FCSTD DOCUMENT  (FreeCAD 1.0R39109 (Git))
Label: tip-etcher_v2]
License: All rights reserved
objects: App::Link×91, App::FeaturePython×20, Assembly::AssemblyLink×10, Assembly::JointGroup×1, Assembly::AssemblyObject×1
EXTERNAL_REF file=power-supply/psu-mount.FCStd obj=Assembly
EXTERNAL_REF file=power-supply/psu-mount.FCStd obj=mount
EXTERNAL_REF file=power-supply/psu-mount.FCStd obj=M3x5_74_Insert
EXTERNAL_REF file=power-supply/psu-mount.FCStd obj=M3x5_74_Insert001
EXTERNAL_REF file=power-supply/psu-mount.FCStd obj=M5x10_Screw
EXTERNAL_REF file=power-supply/psu-mount.FCStd obj=M5x10_Screw002
EXTERNAL_REF file=power-supply/psu-mount.FCStd obj=M5x10_Screw003
EXTERNAL_REF file=power-supply/psu-mount.FCStd obj=M5x10_Screw004
EXTERNAL_REF file=power-supply/psu-mount.FCStd obj=M5x10_Screw005
EXTERNAL_REF file=power-supply/psu-mount.FCStd obj=M5x10_Screw006
EXTERNAL_REF file=power-supply/psu-mount.FCStd obj=M5x10_Screw007
EXTERNAL_REF file=power-supply/psu-mount.FCStd obj=M5x10_Screw008
EXTERNAL_REF file=power-supply/psu-mount.FCStd obj=MW_LRS_50_24
EXTERNAL_REF file=power-supply/psu-mount.FCStd obj=M3x6_Screw
EXTERNAL_REF file=power-supply/psu-mount.FCStd obj=M3x6_Screw001
EXTERNAL_REF file=frame/assembly-frame.FCStd obj=Assembly
EXTERNAL_REF file=frame/assembly-frame.FCStd obj=_020_150mm_v2
EXTERNAL_REF file=frame/assembly-frame.FCStd obj=_020_150mm_v003
EXTERNAL_REF file=frame/assembly-frame.FCStd obj=_020_150mm_v004
EXTERNAL_REF file=frame/assembly-frame.FCStd obj=_020_150mm_v005
EXTERNAL_REF file=frame/assembly-frame.FCStd obj=_020_250mm_v2
EXTERNAL_REF file=frame/assembly-frame.FCStd obj=_020_250mm_v003
EXTERNAL_REF file=frame/assembly-frame.FCStd obj=_020_250mm_v004
EXTERNAL_REF file=frame/assembly-frame.FCStd obj=_020_150mm_v006
EXTERNAL_REF file=frame/assembly-frame.FCStd obj=_020_150mm_v007
EXTERNAL_REF file=frame/assembly-frame.FCStd obj=_020_150mm_v008
EXTERNAL_REF file=frame/assembly-frame.FCStd obj=_020_150mm_v009
EXTERNAL_REF file=frame/L-mount.FCStd obj=Assembly
EXTERNAL_REF file=frame/L-mount.FCStd obj=Body001
EXTERNAL_REF file=frame/L-mount.FCStd obj=M5x10_Screw
EXTERNAL_REF file=frame/L-mount.FCStd obj=M5x10_Screw001
EXTERNAL_REF file=frame/L-mount.FCStd obj=M5x10_Screw002
EXTERNAL_REF file=frame/L-mount.FCStd obj=M5x10_Screw003
EXTERNAL_REF file=frame/L-mount.FCStd obj=M5x10_Screw004
EXTERNAL_REF file=frame/L-mount.FCStd obj=M5x10_Screw005
EXTERNAL_REF file=frame/corner-mount.FCStd obj=Assembly
EXTERNAL_REF file=frame/corner-mount.FCStd obj=M5x10_Screw
EXTERNAL_REF file=frame/corner-mount.FCStd obj=Body001
EXTERNAL_REF file=frame/corner-mount.FCStd obj=M5x10_Screw001
EXTERNAL_REF file=frame/corner-mount.FCStd obj=M5x10_Screw002
EXTERNAL_REF file=frame/corner-mount.FCStd obj=M5x10_Screw003
EXTERNAL_REF file=frame/corner-mount.FCStd obj=M5x10_Screw004
EXTERNAL_REF file=frame/corner-mount.FCStd obj=M5x10_Screw005
EXTERNAL_REF file=mechanism/base.FCStd obj=Body
EXTERNAL_REF file=mechanism/rod.FCStd obj=Body
EXTERNAL_REF file=mechanism/head.FCStd obj=Body
EXTERNAL_REF file=mechanism/top.FCStd obj=Body
EXTERNAL_REF file=mechanism/stm_mount.FCStd obj=Body
EXTERNAL_REF file=mechanism/profile_cover.FCStd obj=Body
EXTERNAL_REF file=mechanism/funnel.FCStd obj=Body
EXTERNAL_REF file=mechanism/bearing_holder.FCStd obj=Body
EXTERNAL_REF file=Screen/Screen_v3.FCStd obj=Body

FEATURE [App::Link] mount  label="mount001"
  LinkedObject = -> <external power-supply/psu-mount.FCStd>#mount
FEATURE [App::Link] M3x5_74_Insert  label="M3x5.74-Insert001"
  LinkPlacement = pos=(48,110,10.0967) rot=(0,0,1;0rad)
  LinkedObject = -> <external power-supply/psu-mount.FCStd>#M3x5_74_Insert
  Placement = pos=(48,110,10.0967) rot=(0,0,1;0rad)
FEATURE [App::Link] M3x5_74_Insert001  label="M3x5.74-Insert002"
  LinkPlacement = pos=(140.5,40,10.0967) rot=(0,0,1;0rad)
  LinkedObject = -> <external power-supply/psu-mount.FCStd>#M3x5_74_Insert001
  Placement = pos=(140.5,40,10.0967) rot=(0,0,1;0rad)
FEATURE [App::Link] M5x10_Screw  label="M5x10-Screw001"
  LinkPlacement = pos=(68.5,10.5,0) rot=(1,0,0;3.14159rad)
  LinkedObject = -> <external power-supply/psu-mount.FCStd>#M5x10_Screw
  Placement = pos=(68.5,10.5,0) rot=(1,0,0;3.14159rad)
FEATURE [App::Link] M5x10_Screw002  label="M5x10-Screw003"
  LinkPlacement = pos=(179.5,58.5,0) rot=(1,0,0;3.14159rad)
  LinkedObject = -> <external power-supply/psu-mount.FCStd>#M5x10_Screw002
  Placement = pos=(179.5,58.5,0) rot=(1,0,0;3.14159rad)
FEATURE [App::Link] M5x10_Screw003  label="M5x10-Screw004"
  LinkPlacement = pos=(179.5,91.5,0) rot=(1,0,0;3.14159rad)
  LinkedObject = -> <external power-supply/psu-mount.FCStd>#M5x10_Screw003
  Placement = pos=(179.5,91.5,0) rot=(1,0,0;3.14159rad)
FEATURE [App::Link] M5x10_Screw004  label="M5x10-Screw005"
  LinkPlacement = pos=(121.5,139.5,0) rot=(1,0,0;3.14159rad)
  LinkedObject = -> <external power-supply/psu-mount.FCStd>#M5x10_Screw004
  Placement = pos=(121.5,139.5,0) rot=(1,0,0;3.14159rad)
FEATURE [App::Link] M5x10_Screw005  label="M5x10-Screw006"
  LinkPlacement = pos=(68.5,139.5,0) rot=(1,0,0;3.14159rad)
  LinkedObject = -> <external power-supply/psu-mount.FCStd>#M5x10_Screw005
  Placement = pos=(68.5,139.5,0) rot=(1,0,0;3.14159rad)
FEATURE [App::Link] M5x10_Screw006  label="M5x10-Screw007"
  LinkPlacement = pos=(10.5,58.5,0) rot=(1,0,0;3.14159rad)
  LinkedObject = -> <external power-supply/psu-mount.FCStd>#M5x10_Screw006
  Placement = pos=(10.5,58.5,0) rot=(1,0,0;3.14159rad)
FEATURE [App::Link] M5x10_Screw007  label="M5x10-Screw008"
  LinkPlacement = pos=(10.5,91.5,0) rot=(1,0,0;3.14159rad)
  LinkedObject = -> <external power-supply/psu-mount.FCStd>#M5x10_Screw007
  Placement = pos=(10.5,91.5,0) rot=(1,0,0;3.14159rad)
FEATURE [App::Link] M5x10_Screw008  label="M5x10-Screw009"
  LinkPlacement = pos=(121.5,10.5,0) rot=(1,0,0;3.14159rad)
  LinkedObject = -> <external power-supply/psu-mount.FCStd>#M5x10_Screw008
  Placement = pos=(121.5,10.5,0) rot=(1,0,0;3.14159rad)
FEATURE [App::Link] MW_LRS_50_24  label="MW LRS-50-025"
  LinkPlacement = pos=(43.5,33.5,10) rot=(1,0,0;1.5708rad)
  LinkedObject = -> <external power-supply/psu-mount.FCStd>#MW_LRS_50_24
  Placement = pos=(43.5,33.5,10) rot=(1,0,0;1.5708rad)
FEATURE [App::Link] M3x6_Screw  label="M3x6-Screw001"
  LinkPlacement = pos=(48,110,11) rot=(0,0,1;4.71239rad)
  LinkedObject = -> <external power-supply/psu-mount.FCStd>#M3x6_Screw
  Placement = pos=(48,110,11) rot=(0,0,1;4.71239rad)
FEATURE [App::Link] M3x6_Screw001  label="M3x6-Screw002"
  LinkPlacement = pos=(140.5,40,11) rot=(0,0,-1;1.5708rad)
  LinkedObject = -> <external power-supply/psu-mount.FCStd>#M3x6_Screw001
  Placement = pos=(140.5,40,11) rot=(0,0,-1;1.5708rad)
FEATURE [Assembly::AssemblyLink] psu_mount  label="psu-mount"
  Group = -> [mount,M3x5_74_Insert,M3x5_74_Insert001,M5x10_Screw,M5x10_Screw002,M5x10_Screw003,M5x10_Screw004,M5x10_Screw005,M5x10_Screw006,M5x10_Screw007,M5x10_Screw008,MW_LRS_50_24,M3x6_Screw,M3x6_Screw001]
  LinkedObject = -> <external power-supply/psu-mount.FCStd>#Assembly
  Origin = -> Origin001
  Placement = pos=(-9.50002,14,-3.8147e-06) rot=(1,0,0;1.5708rad)
  Rigid = true
FEATURE [App::Link] _020_150mm_v2  label="2020_150mm_001"
  LinkedObject = -> <external frame/assembly-frame.FCStd>#_020_150mm_v2
FEATURE [App::Link] _020_150mm_v003  label="2020_150mm_002"
  LinkPlacement = pos=(160,1.8e-15,140) rot=(0,-1,0;1.5708rad)
  LinkedObject = -> <external frame/assembly-frame.FCStd>#_020_150mm_v003
  Placement = pos=(160,1.8e-15,140) rot=(0,-1,0;1.5708rad)
FEATURE [App::Link] _020_150mm_v004  label="2020_150mm_003"
  LinkPlacement = pos=(170,3.64e-14,-2.49e-14) rot=(0,0,1;0rad)
  LinkedObject = -> <external frame/assembly-frame.FCStd>#_020_150mm_v004
  Placement = pos=(170,3.64e-14,-2.49e-14) rot=(0,0,1;0rad)
FEATURE [App::Link] _020_150mm_v005  label="2020_150mm_004"
  LinkPlacement = pos=(160,2.7e-15,10) rot=(0,1,0;4.71239rad)
  LinkedObject = -> <external frame/assembly-frame.FCStd>#_020_150mm_v005
  Placement = pos=(160,2.7e-15,10) rot=(0,1,0;4.71239rad)
FEATURE [App::Link] _020_250mm_v2  label="2020_250mm_001"
  LinkPlacement = pos=(-1.101e-13,-260,10) rot=(-1,0,0;1.5708rad)
  LinkedObject = -> <external frame/assembly-frame.FCStd>#_020_250mm_v2
  Placement = pos=(-1.101e-13,-260,10) rot=(-1,0,0;1.5708rad)
FEATURE [App::Link] _020_250mm_v003  label="2020_250mm_002"
  LinkPlacement = pos=(1.11e-13,-260,140) rot=(1,0,0;4.71239rad)
  LinkedObject = -> <external frame/assembly-frame.FCStd>#_020_250mm_v003
  Placement = pos=(1.11e-13,-260,140) rot=(1,0,0;4.71239rad)
FEATURE [App::Link] _020_250mm_v004  label="2020_250mm_003"
  LinkPlacement = pos=(170,-260,10) rot=(-1,0,0;1.5708rad)
  LinkedObject = -> <external frame/assembly-frame.FCStd>#_020_250mm_v004
  Placement = pos=(170,-260,10) rot=(-1,0,0;1.5708rad)
FEATURE [App::Link] _020_150mm_v006  label="2020_150mm_005"
  LinkPlacement = pos=(1.814e-13,-270,7.13e-14) rot=(0,0,1;0rad)
  LinkedObject = -> <external frame/assembly-frame.FCStd>#_020_150mm_v006
  Placement = pos=(1.814e-13,-270,7.13e-14) rot=(0,0,1;0rad)
FEATURE [App::Link] _020_150mm_v007  label="2020_150mm_006"
  LinkPlacement = pos=(10,-270,140) rot=(0,1,0;1.5708rad)
  LinkedObject = -> <external frame/assembly-frame.FCStd>#_020_150mm_v007
  Placement = pos=(10,-270,140) rot=(0,1,0;1.5708rad)
FEATURE [App::Link] _020_150mm_v008  label="2020_150mm_007"
  LinkPlacement = pos=(170,-270,150) rot=(1,0,0;3.14159rad)
  LinkedObject = -> <external frame/assembly-frame.FCStd>#_020_150mm_v008
  Placement = pos=(170,-270,150) rot=(1,0,0;3.14159rad)
FEATURE [App::Link] _020_150mm_v009  label="2020_150mm_008"
  LinkPlacement = pos=(10,-270,10) rot=(0,1,0;1.5708rad)
  LinkedObject = -> <external frame/assembly-frame.FCStd>#_020_150mm_v009
  Placement = pos=(10,-270,10) rot=(0,1,0;1.5708rad)
FEATURE [Assembly::AssemblyLink] frame
  Group = -> [_020_150mm_v2,_020_150mm_v003,_020_150mm_v004,_020_150mm_v005,_020_250mm_v2,_020_250mm_v003,_020_250mm_v004,_020_150mm_v006,_020_150mm_v007,_020_150mm_v008,_020_150mm_v009]
  LinkedObject = -> <external frame/assembly-frame.FCStd>#Assembly
  Origin = -> Origin002
  Placement = pos=(-1.52588e-05,1.52588e-05,-3.8147e-06) rot=(0,0,1;0rad)
  Rigid = true
FEATURE [App::Link] Body001
  LinkedObject = -> <external frame/L-mount.FCStd>#Body001
FEATURE [App::Link] M5x10_Screw009  label="M5x10-Screw010"
  LinkPlacement = pos=(14,34,0) rot=(1,0,0;3.14159rad)
  LinkedObject = -> <external frame/L-mount.FCStd>#M5x10_Screw
  Placement = pos=(14,34,0) rot=(1,0,0;3.14159rad)
FEATURE [App::Link] M5x10_Screw001  label="M5x10-Screw002"
  LinkPlacement = pos=(28.2,34,14) rot=(0.57735,0.57735,0.57735;2.0944rad)
  LinkedObject = -> <external frame/L-mount.FCStd>#M5x10_Screw001
  Placement = pos=(28.2,34,14) rot=(0.57735,0.57735,0.57735;2.0944rad)
FEATURE [App::Link] M5x10_Screw010  label="M5x10-Screw011"
  LinkPlacement = pos=(14,0,34) rot=(1,0,0;1.5708rad)
  LinkedObject = -> <external frame/L-mount.FCStd>#M5x10_Screw002
  Placement = pos=(14,0,34) rot=(1,0,0;1.5708rad)
FEATURE [App::Link] M5x10_Screw011  label="M5x10-Screw012"
  LinkPlacement = pos=(-0.2,34,14) rot=(0.57735,-0.57735,-0.57735;2.0944rad)
  LinkedObject = -> <external frame/L-mount.FCStd>#M5x10_Screw003
  Placement = pos=(-0.2,34,14) rot=(0.57735,-0.57735,-0.57735;2.0944rad)
FEATURE [App::Link] M5x10_Screw012  label="M5x10-Screw013"
  LinkPlacement = pos=(-0.2,14,34) rot=(0.57735,-0.57735,-0.57735;2.0944rad)
  LinkedObject = -> <external frame/L-mount.FCStd>#M5x10_Screw004
  Placement = pos=(-0.2,14,34) rot=(0.57735,-0.57735,-0.57735;2.0944rad)
FEATURE [App::Link] M5x10_Screw013  label="M5x10-Screw014"
  LinkPlacement = pos=(28.2,14,34) rot=(0.57735,0.57735,0.57735;2.0944rad)
  LinkedObject = -> <external frame/L-mount.FCStd>#M5x10_Screw005
  Placement = pos=(28.2,14,34) rot=(0.57735,0.57735,0.57735;2.0944rad)
FEATURE [Assembly::AssemblyLink] l_mount  label="l-mount"
  Group = -> [Body001,M5x10_Screw009,M5x10_Screw001,M5x10_Screw010,M5x10_Screw011,M5x10_Screw012,M5x10_Screw013]
  LinkedObject = -> <external frame/L-mount.FCStd>#Assembly
  Origin = -> Origin003
  Placement = pos=(184,-256,154) rot=(0.707107,-0.707107,0;3.14159rad)
  Rigid = true
FEATURE [App::Link] M5x10_Screw014  label="M5x10-Screw015"
  LinkPlacement = pos=(34,-14,-3.1e-15) rot=(1,0,0;3.14159rad)
  LinkedObject = -> <external frame/corner-mount.FCStd>#M5x10_Screw
  Placement = pos=(34,-14,-3.1e-15) rot=(1,0,0;3.14159rad)
FEATURE [App::Link] Body002
  LinkedObject = -> <external frame/corner-mount.FCStd>#Body001
FEATURE [App::Link] M5x10_Screw015  label="M5x10-Screw016"
  LinkPlacement = pos=(0,-34,14) rot=(-0.707107,0,0.707107;3.14159rad)
  LinkedObject = -> <external frame/corner-mount.FCStd>#M5x10_Screw001
  Placement = pos=(0,-34,14) rot=(-0.707107,0,0.707107;3.14159rad)
FEATURE [App::Link] M5x10_Screw016  label="M5x10-Screw017"
  LinkPlacement = pos=(0,-14,34) rot=(0.707107,0,-0.707107;3.14159rad)
  LinkedObject = -> <external frame/corner-mount.FCStd>#M5x10_Screw002
  Placement = pos=(0,-14,34) rot=(0.707107,0,-0.707107;3.14159rad)
FEATURE [App::Link] M5x10_Screw017  label="M5x10-Screw018"
  LinkPlacement = pos=(14,-7.5e-15,34) rot=(-1,0,0;1.5708rad)
  LinkedObject = -> <external frame/corner-mount.FCStd>#M5x10_Screw003
  Placement = pos=(14,-7.5e-15,34) rot=(-1,0,0;1.5708rad)
FEATURE [App::Link] M5x10_Screw018  label="M5x10-Screw019"
  LinkPlacement = pos=(34,-3.1e-15,14) rot=(-1,0,0;1.5708rad)
  LinkedObject = -> <external frame/corner-mount.FCStd>#M5x10_Screw004
  Placement = pos=(34,-3.1e-15,14) rot=(-1,0,0;1.5708rad)
FEATURE [App::Link] M5x10_Screw019  label="M5x10-Screw020"
  LinkPlacement = pos=(14,-34,-7.6e-15) rot=(1,0,0;3.14159rad)
  LinkedObject = -> <external frame/corner-mount.FCStd>#M5x10_Screw005
  Placement = pos=(14,-34,-7.6e-15) rot=(1,0,0;3.14159rad)
FEATURE [Assembly::AssemblyLink] corner_mount  label="corner-mount"
  Group = -> [M5x10_Screw014,Body002,M5x10_Screw015,M5x10_Screw016,M5x10_Screw017,M5x10_Screw018,M5x10_Screw019]
  LinkedObject = -> <external frame/corner-mount.FCStd>#Assembly
  Origin = -> Origin004
  Placement = pos=(-14,-284,154) rot=(0.57735,-0.57735,-0.57735;4.18879rad)
  Rigid = true
FEATURE [App::Link] Body003
  LinkedObject = -> <external frame/L-mount.FCStd>#Body001
FEATURE [App::Link] M5x10_Screw020  label="M5x10-Screw021"
  LinkPlacement = pos=(14,34,0) rot=(1,0,0;3.14159rad)
  LinkedObject = -> <external frame/L-mount.FCStd>#M5x10_Screw
  Placement = pos=(14,34,0) rot=(1,0,0;3.14159rad)
FEATURE [App::Link] M5x10_Screw021  label="M5x10-Screw022"
  LinkPlacement = pos=(28.2,34,14) rot=(0.57735,0.57735,0.57735;2.0944rad)
  LinkedObject = -> <external frame/L-mount.FCStd>#M5x10_Screw001
  Placement = pos=(28.2,34,14) rot=(0.57735,0.57735,0.57735;2.0944rad)
FEATURE [App::Link] M5x10_Screw022  label="M5x10-Screw023"
  LinkPlacement = pos=(14,0,34) rot=(1,0,0;1.5708rad)
  LinkedObject = -> <external frame/L-mount.FCStd>#M5x10_Screw002
  Placement = pos=(14,0,34) rot=(1,0,0;1.5708rad)
FEATURE [App::Link] M5x10_Screw023  label="M5x10-Screw024"
  LinkPlacement = pos=(-0.2,34,14) rot=(0.57735,-0.57735,-0.57735;2.0944rad)
  LinkedObject = -> <external frame/L-mount.FCStd>#M5x10_Screw003
  Placement = pos=(-0.2,34,14) rot=(0.57735,-0.57735,-0.57735;2.0944rad)
FEATURE [App::Link] M5x10_Screw024  label="M5x10-Screw025"
  LinkPlacement = pos=(-0.2,14,34) rot=(0.57735,-0.57735,-0.57735;2.0944rad)
  LinkedObject = -> <external frame/L-mount.FCStd>#M5x10_Screw004
  Placement = pos=(-0.2,14,34) rot=(0.57735,-0.57735,-0.57735;2.0944rad)
FEATURE [App::Link] M5x10_Screw025  label="M5x10-Screw026"
  LinkPlacement = pos=(28.2,14,34) rot=(0.57735,0.57735,0.57735;2.0944rad)
  LinkedObject = -> <external frame/L-mount.FCStd>#M5x10_Screw005
  Placement = pos=(28.2,14,34) rot=(0.57735,0.57735,0.57735;2.0944rad)
FEATURE [Assembly::AssemblyLink] l_mount001  label="l-mount001"
  Group = -> [Body003,M5x10_Screw020,M5x10_Screw021,M5x10_Screw022,M5x10_Screw023,M5x10_Screw024,M5x10_Screw025]
  LinkedObject = -> <external frame/L-mount.FCStd>#Assembly
  Origin = -> Origin005
  Placement = pos=(184,-14,154) rot=(-0.57735,-0.57735,0.57735;2.0944rad)
  Rigid = true
FEATURE [App::Link] M5x10_Screw032  label="M5x10-Screw033"
  LinkPlacement = pos=(34,-14,-3.1e-15) rot=(1,0,0;3.14159rad)
  LinkedObject = -> <external frame/corner-mount.FCStd>#M5x10_Screw
  Placement = pos=(34,-14,-3.1e-15) rot=(1,0,0;3.14159rad)
FEATURE [App::Link] Body005
  LinkedObject = -> <external frame/corner-mount.FCStd>#Body001
FEATURE [App::Link] M5x10_Screw033  label="M5x10-Screw034"
  LinkPlacement = pos=(0,-34,14) rot=(-0.707107,0,0.707107;3.14159rad)
  LinkedObject = -> <external frame/corner-mount.FCStd>#M5x10_Screw001
  Placement = pos=(0,-34,14) rot=(-0.707107,0,0.707107;3.14159rad)
FEATURE [App::Link] M5x10_Screw034  label="M5x10-Screw035"
  LinkPlacement = pos=(0,-14,34) rot=(0.707107,0,-0.707107;3.14159rad)
  LinkedObject = -> <external frame/corner-mount.FCStd>#M5x10_Screw002
  Placement = pos=(0,-14,34) rot=(0.707107,0,-0.707107;3.14159rad)
FEATURE [App::Link] M5x10_Screw035  label="M5x10-Screw036"
  LinkPlacement = pos=(14,-7.5e-15,34) rot=(-1,0,0;1.5708rad)
  LinkedObject = -> <external frame/corner-mount.FCStd>#M5x10_Screw003
  Placement = pos=(14,-7.5e-15,34) rot=(-1,0,0;1.5708rad)
FEATURE [App::Link] M5x10_Screw036  label="M5x10-Screw037"
  LinkPlacement = pos=(34,-3.1e-15,14) rot=(-1,0,0;1.5708rad)
  LinkedObject = -> <external frame/corner-mount.FCStd>#M5x10_Screw004
  Placement = pos=(34,-3.1e-15,14) rot=(-1,0,0;1.5708rad)
FEATURE [App::Link] M5x10_Screw037  label="M5x10-Screw038"
  LinkPlacement = pos=(14,-34,-7.6e-15) rot=(1,0,0;3.14159rad)
  LinkedObject = -> <external frame/corner-mount.FCStd>#M5x10_Screw005
  Placement = pos=(14,-34,-7.6e-15) rot=(1,0,0;3.14159rad)
FEATURE [Assembly::AssemblyLink] corner_mount002  label="corner-mount002"
  Group = -> [M5x10_Screw032,Body005,M5x10_Screw033,M5x10_Screw034,M5x10_Screw035,M5x10_Screw036,M5x10_Screw037]
  LinkedObject = -> <external frame/corner-mount.FCStd>#Assembly
  Origin = -> Origin007
  Placement = pos=(-14,-284,-4) rot=(1,0,0;4.71239rad)
  Rigid = true
FEATURE [App::Link] M5x10_Screw038  label="M5x10-Screw039"
  LinkPlacement = pos=(34,-14,-3.1e-15) rot=(1,0,0;3.14159rad)
  LinkedObject = -> <external frame/corner-mount.FCStd>#M5x10_Screw
  Placement = pos=(34,-14,-3.1e-15) rot=(1,0,0;3.14159rad)
FEATURE [App::Link] Body006
  LinkedObject = -> <external frame/corner-mount.FCStd>#Body001
FEATURE [App::Link] M5x10_Screw039  label="M5x10-Screw040"
  LinkPlacement = pos=(0,-34,14) rot=(-0.707107,0,0.707107;3.14159rad)
  LinkedObject = -> <external frame/corner-mount.FCStd>#M5x10_Screw001
  Placement = pos=(0,-34,14) rot=(-0.707107,0,0.707107;3.14159rad)
FEATURE [App::Link] M5x10_Screw040  label="M5x10-Screw041"
  LinkPlacement = pos=(0,-14,34) rot=(0.707107,0,-0.707107;3.14159rad)
  LinkedObject = -> <external frame/corner-mount.FCStd>#M5x10_Screw002
  Placement = pos=(0,-14,34) rot=(0.707107,0,-0.707107;3.14159rad)
FEATURE [App::Link] M5x10_Screw041  label="M5x10-Screw042"
  LinkPlacement = pos=(14,-7.5e-15,34) rot=(-1,0,0;1.5708rad)
  LinkedObject = -> <external frame/corner-mount.FCStd>#M5x10_Screw003
  Placement = pos=(14,-7.5e-15,34) rot=(-1,0,0;1.5708rad)
FEATURE [App::Link] M5x10_Screw042  label="M5x10-Screw043"
  LinkPlacement = pos=(34,-3.1e-15,14) rot=(-1,0,0;1.5708rad)
  LinkedObject = -> <external frame/corner-mount.FCStd>#M5x10_Screw004
  Placement = pos=(34,-3.1e-15,14) rot=(-1,0,0;1.5708rad)
FEATURE [App::Link] M5x10_Screw043  label="M5x10-Screw044"
  LinkPlacement = pos=(14,-34,-7.6e-15) rot=(1,0,0;3.14159rad)
  LinkedObject = -> <external frame/corner-mount.FCStd>#M5x10_Screw005
  Placement = pos=(14,-34,-7.6e-15) rot=(1,0,0;3.14159rad)
FEATURE [Assembly::AssemblyLink] corner_mount003  label="corner-mount003"
  Group = -> [M5x10_Screw038,Body006,M5x10_Screw039,M5x10_Screw040,M5x10_Screw041,M5x10_Screw042,M5x10_Screw043]
  LinkedObject = -> <external frame/corner-mount.FCStd>#Assembly
  Origin = -> Origin008
  Placement = pos=(-14,14,154) rot=(1,0,0;1.5708rad)
  Rigid = true
FEATURE [App::Link] M5x10_Screw044  label="M5x10-Screw045"
  LinkPlacement = pos=(34,-14,-3.1e-15) rot=(1,0,0;3.14159rad)
  LinkedObject = -> <external frame/corner-mount.FCStd>#M5x10_Screw
  Placement = pos=(34,-14,-3.1e-15) rot=(1,0,0;3.14159rad)
FEATURE [App::Link] Body007
  LinkedObject = -> <external frame/corner-mount.FCStd>#Body001
FEATURE [App::Link] M5x10_Screw045  label="M5x10-Screw046"
  LinkPlacement = pos=(0,-34,14) rot=(-0.707107,0,0.707107;3.14159rad)
  LinkedObject = -> <external frame/corner-mount.FCStd>#M5x10_Screw001
  Placement = pos=(0,-34,14) rot=(-0.707107,0,0.707107;3.14159rad)
FEATURE [App::Link] M5x10_Screw046  label="M5x10-Screw047"
  LinkPlacement = pos=(0,-14,34) rot=(0.707107,0,-0.707107;3.14159rad)
  LinkedObject = -> <external frame/corner-mount.FCStd>#M5x10_Screw002
  Placement = pos=(0,-14,34) rot=(0.707107,0,-0.707107;3.14159rad)
FEATURE [App::Link] M5x10_Screw047  label="M5x10-Screw048"
  LinkPlacement = pos=(14,-7.5e-15,34) rot=(-1,0,0;1.5708rad)
  LinkedObject = -> <external frame/corner-mount.FCStd>#M5x10_Screw003
  Placement = pos=(14,-7.5e-15,34) rot=(-1,0,0;1.5708rad)
FEATURE [App::Link] M5x10_Screw048  label="M5x10-Screw049"
  LinkPlacement = pos=(34,-3.1e-15,14) rot=(-1,0,0;1.5708rad)
  LinkedObject = -> <external frame/corner-mount.FCStd>#M5x10_Screw004
  Placement = pos=(34,-3.1e-15,14) rot=(-1,0,0;1.5708rad)
FEATURE [App::Link] M5x10_Screw049  label="M5x10-Screw050"
  LinkPlacement = pos=(14,-34,-7.6e-15) rot=(1,0,0;3.14159rad)
  LinkedObject = -> <external frame/corner-mount.FCStd>#M5x10_Screw005
  Placement = pos=(14,-34,-7.6e-15) rot=(1,0,0;3.14159rad)
FEATURE [Assembly::AssemblyLink] corner_mount004  label="corner-mount004"
  Group = -> [M5x10_Screw044,Body007,M5x10_Screw045,M5x10_Screw046,M5x10_Screw047,M5x10_Screw048,M5x10_Screw049]
  LinkedObject = -> <external frame/corner-mount.FCStd>#Assembly
  Origin = -> Origin009
  Placement = pos=(184,-284,-4) rot=(0,0,1;3.14159rad)
  Rigid = true
FEATURE [App::Link] M5x10_Screw050  label="M5x10-Screw051"
  LinkPlacement = pos=(34,-14,-3.1e-15) rot=(1,0,0;3.14159rad)
  LinkedObject = -> <external frame/corner-mount.FCStd>#M5x10_Screw
  Placement = pos=(34,-14,-3.1e-15) rot=(1,0,0;3.14159rad)
FEATURE [App::Link] Body008
  LinkedObject = -> <external frame/corner-mount.FCStd>#Body001
FEATURE [App::Link] M5x10_Screw051  label="M5x10-Screw052"
  LinkPlacement = pos=(0,-34,14) rot=(-0.707107,0,0.707107;3.14159rad)
  LinkedObject = -> <external frame/corner-mount.FCStd>#M5x10_Screw001
  Placement = pos=(0,-34,14) rot=(-0.707107,0,0.707107;3.14159rad)
FEATURE [App::Link] M5x10_Screw052  label="M5x10-Screw053"
  LinkPlacement = pos=(0,-14,34) rot=(0.707107,0,-0.707107;3.14159rad)
  LinkedObject = -> <external frame/corner-mount.FCStd>#M5x10_Screw002
  Placement = pos=(0,-14,34) rot=(0.707107,0,-0.707107;3.14159rad)
FEATURE [App::Link] M5x10_Screw053  label="M5x10-Screw054"
  LinkPlacement = pos=(14,-7.5e-15,34) rot=(-1,0,0;1.5708rad)
  LinkedObject = -> <external frame/corner-mount.FCStd>#M5x10_Screw003
  Placement = pos=(14,-7.5e-15,34) rot=(-1,0,0;1.5708rad)
FEATURE [App::Link] M5x10_Screw054  label="M5x10-Screw055"
  LinkPlacement = pos=(34,-3.1e-15,14) rot=(-1,0,0;1.5708rad)
  LinkedObject = -> <external frame/corner-mount.FCStd>#M5x10_Screw004
  Placement = pos=(34,-3.1e-15,14) rot=(-1,0,0;1.5708rad)
FEATURE [App::Link] M5x10_Screw055  label="M5x10-Screw056"
  LinkPlacement = pos=(14,-34,-7.6e-15) rot=(1,0,0;3.14159rad)
  LinkedObject = -> <external frame/corner-mount.FCStd>#M5x10_Screw005
  Placement = pos=(14,-34,-7.6e-15) rot=(1,0,0;3.14159rad)
FEATURE [Assembly::AssemblyLink] corner_mount005  label="corner-mount005"
  Group = -> [M5x10_Screw050,Body008,M5x10_Screw051,M5x10_Screw052,M5x10_Screw053,M5x10_Screw054,M5x10_Screw055]
  LinkedObject = -> <external frame/corner-mount.FCStd>#Assembly
  Origin = -> Origin010
  Placement = pos=(184,14,-4) rot=(0,0,-1;1.5708rad)
  Rigid = true
FEATURE [App::FeaturePython] GroundedJoint  # Assembly grounded joint (typed FeaturePython)
  ObjectToGround = -> frame
  Placement = pos=(-1.52588e-05,1.52588e-05,-3.8147e-06) rot=(0,0,1;0rad)
FEATURE [App::FeaturePython] Joint  label="Fixed"  # Assembly joint (typed FeaturePython)
  Activated = true
  AngleMax = 0
  AngleMin = 0
  Detach1 = false
  Detach2 = false
  Distance = 0
  Distance2 = 0
  EnableAngleMax = false
  EnableAngleMin = false
  EnableLengthMax = false
  EnableLengthMin = false
  JointType = 0 (Fixed)
  LengthMax = 0
  LengthMin = 0
  Offset2 = pos=(0,0,7) rot=(0,0,1;0rad)
  Placement1 = pos=(14,4,4) rot=(-0.707107,0,0.707107;3.14159rad)
  Placement2 = pos=(10,0,0) rot=(-0.57735,-0.57735,0.57735;4.18879rad)
  Reference1 = -> Assembly [l_mount.Body001.Edge61,l_mount.Body001.Edge61]
  Reference2 = -> Assembly [frame._020_150mm_v008.Edge72,frame._020_150mm_v008.Edge72]
FEATURE [App::FeaturePython] Joint001  label="Fixed001"  # Assembly joint (typed FeaturePython)
  Activated = true
  AngleMax = 0
  AngleMin = 0
  Detach1 = false
  Detach2 = false
  Distance = 0
  Distance2 = 0
  EnableAngleMax = false
  EnableAngleMin = false
  EnableLengthMax = false
  EnableLengthMin = false
  JointType = 0 (Fixed)
  LengthMax = 0
  LengthMin = 0
  Offset2 = pos=(0,0,17) rot=(0,0,1;1.5708rad)
  Placement1 = pos=(4,4,4) rot=(-0.707107,0,0.707107;3.14159rad)
  Placement2 = pos=(10,-10,150) rot=(-1,0,0;4.71239rad)
  Reference1 = -> Assembly [l_mount001.Body003.Edge61,l_mount001.Body003.Vertex44]
  Reference2 = -> Assembly [frame._020_150mm_v004.Edge14,frame._020_150mm_v004.Edge14]
FEATURE [App::FeaturePython] Joint002  label="Fixed002"  # Assembly joint (typed FeaturePython)
  Activated = true
  AngleMax = 0
  AngleMin = 0
  Detach1 = false
  Detach2 = false
  Distance = 0
  Distance2 = 0
  EnableAngleMax = false
  EnableAngleMin = false
  EnableLengthMax = false
  EnableLengthMin = false
  JointType = 0 (Fixed)
  LengthMax = 0
  LengthMin = 0
  Offset1 = pos=(0,-2,0) rot=(0,0,1;0rad)
  Placement1 = pos=(181,110,0) rot=(-0.707107,0,0.707107;3.14159rad)
  Placement2 = pos=(28,44,12.5) rot=(0,0,1;0rad)
  Reference1 = -> Assembly [psu_mount.mount.Edge19,psu_mount.mount.Edge19]
  Reference2 = -> Assembly [l_mount001.Body003.Edge30,l_mount001.Body003.Edge30]
FEATURE [App::FeaturePython] Joint003  label="Fixed003"  # Assembly joint (typed FeaturePython)
  Activated = true
  AngleMax = 0
  AngleMin = 0
  Detach1 = false
  Detach2 = false
  Distance = 0
  Distance2 = 0
  EnableAngleMax = false
  EnableAngleMin = false
  EnableLengthMax = false
  EnableLengthMin = false
  JointType = 0 (Fixed)
  LengthMax = 0
  LengthMin = 0
  Offset2 = pos=(0,0,-17) rot=(0,0,-1;1.5708rad)
  Placement1 = pos=(24,-4,4) rot=(0.707107,0,0.707107;3.14159rad)
  Placement2 = pos=(10,-10,0) rot=(-0.57735,-0.57735,0.57735;2.0944rad)
  Reference1 = -> Assembly [corner_mount002.Body005.Edge46,corner_mount002.Body005.Edge46]
  Reference2 = -> Assembly [frame._020_150mm_v006.Edge107,frame._020_150mm_v006.Edge107]
FEATURE [App::FeaturePython] Joint004  label="Fixed004"  # Assembly joint (typed FeaturePython)
  Activated = true
  AngleMax = 0
  AngleMin = 0
  Detach1 = false
  Detach2 = false
  Distance = 0
  Distance2 = 0
  EnableAngleMax = false
  EnableAngleMin = false
  EnableLengthMax = false
  EnableLengthMin = false
  JointType = 0 (Fixed)
  LengthMax = 0
  LengthMin = 0
  Offset2 = pos=(0,0,17) rot=(0,0,1;0rad)
  Placement1 = pos=(4,-4,24) rot=(0,1,0;3.14159rad)
  Placement2 = pos=(-10,10,150) rot=(0.57735,0.57735,0.57735;4.18879rad)
  Reference1 = -> Assembly [corner_mount.Body002.Edge51,corner_mount.Body002.Edge51]
  Reference2 = -> Assembly [frame._020_150mm_v006.Edge38,frame._020_150mm_v006.Edge38]
FEATURE [App::FeaturePython] Joint005  label="Fixed005"  # Assembly joint (typed FeaturePython)
  Activated = true
  AngleMax = 0
  AngleMin = 0
  Detach1 = false
  Detach2 = false
  Distance = 0
  Distance2 = 0
  EnableAngleMax = false
  EnableAngleMin = false
  EnableLengthMax = false
  EnableLengthMin = false
  JointType = 0 (Fixed)
  LengthMax = 0
  LengthMin = 0
  Offset2 = pos=(0,0,-37) rot=(0,0,-1;1.5708rad)
  Placement1 = pos=(4,-4,44) rot=(0,1,0;3.14159rad)
  Placement2 = pos=(-10,-30,150) rot=(0,0.707107,0.707107;3.14159rad)
  Reference1 = -> Assembly [corner_mount003.Body006.Edge51,corner_mount003.Body006.Vertex22]
  Reference2 = -> Assembly [frame._020_150mm_v2.Edge28,frame._020_150mm_v2.Edge28]
FEATURE [App::FeaturePython] Joint007  label="Fixed007"  # Assembly joint (typed FeaturePython)
  Activated = true
  AngleMax = 0
  AngleMin = 0
  Detach1 = false
  Detach2 = false
  Distance = 0
  Distance2 = 0
  EnableAngleMax = false
  EnableAngleMin = false
  EnableLengthMax = false
  EnableLengthMin = false
  JointType = 0 (Fixed)
  LengthMax = 0
  LengthMin = 0
  Offset2 = pos=(0,0,17) rot=(0,0,1;3.14159rad)
  Placement1 = pos=(24,-4,4) rot=(0.707107,0,0.707107;3.14159rad)
  Placement2 = pos=(10,-10,0) rot=(-0.57735,0.57735,-0.57735;4.18879rad)
  Reference1 = -> Assembly [corner_mount005.Body008.Edge46,corner_mount005.Body008.Edge46]
  Reference2 = -> Assembly [frame._020_150mm_v004.Edge72,frame._020_150mm_v004.Edge72]
FEATURE [App::Link] M5x10_Screw056  label="M5x10-Screw057"
  LinkPlacement = pos=(34,-14,-3.1e-15) rot=(1,0,0;3.14159rad)
  LinkedObject = -> <external frame/corner-mount.FCStd>#M5x10_Screw
  Placement = pos=(34,-14,-3.1e-15) rot=(1,0,0;3.14159rad)
FEATURE [App::Link] Body009
  LinkedObject = -> <external frame/corner-mount.FCStd>#Body001
FEATURE [App::Link] M5x10_Screw057  label="M5x10-Screw058"
  LinkPlacement = pos=(0,-34,14) rot=(-0.707107,0,0.707107;3.14159rad)
  LinkedObject = -> <external frame/corner-mount.FCStd>#M5x10_Screw001
  Placement = pos=(0,-34,14) rot=(-0.707107,0,0.707107;3.14159rad)
FEATURE [App::Link] M5x10_Screw058  label="M5x10-Screw059"
  LinkPlacement = pos=(0,-14,34) rot=(0.707107,0,-0.707107;3.14159rad)
  LinkedObject = -> <external frame/corner-mount.FCStd>#M5x10_Screw002
  Placement = pos=(0,-14,34) rot=(0.707107,0,-0.707107;3.14159rad)
FEATURE [App::Link] M5x10_Screw059  label="M5x10-Screw060"
  LinkPlacement = pos=(14,-7.5e-15,34) rot=(-1,0,0;1.5708rad)
  LinkedObject = -> <external frame/corner-mount.FCStd>#M5x10_Screw003
  Placement = pos=(14,-7.5e-15,34) rot=(-1,0,0;1.5708rad)
FEATURE [App::Link] M5x10_Screw060  label="M5x10-Screw061"
  LinkPlacement = pos=(34,-3.1e-15,14) rot=(-1,0,0;1.5708rad)
  LinkedObject = -> <external frame/corner-mount.FCStd>#M5x10_Screw004
  Placement = pos=(34,-3.1e-15,14) rot=(-1,0,0;1.5708rad)
FEATURE [App::Link] M5x10_Screw061  label="M5x10-Screw062"
  LinkPlacement = pos=(14,-34,-7.6e-15) rot=(1,0,0;3.14159rad)
  LinkedObject = -> <external frame/corner-mount.FCStd>#M5x10_Screw005
  Placement = pos=(14,-34,-7.6e-15) rot=(1,0,0;3.14159rad)
FEATURE [Assembly::AssemblyLink] corner_mount006  label="corner-mount006"
  Group = -> [M5x10_Screw056,Body009,M5x10_Screw057,M5x10_Screw058,M5x10_Screw059,M5x10_Screw060,M5x10_Screw061]
  LinkedObject = -> <external frame/corner-mount.FCStd>#Assembly
  Origin = -> Origin011
  Placement = pos=(-14,14,-4) rot=(0,0,1;0rad)
  Rigid = true
FEATURE [App::FeaturePython] Joint008  label="Fixed008"  # Assembly joint (typed FeaturePython)
  Activated = true
  AngleMax = 0
  AngleMin = 0
  Detach1 = false
  Detach2 = false
  Distance = 0
  Distance2 = 0
  EnableAngleMax = false
  EnableAngleMin = false
  EnableLengthMax = false
  EnableLengthMin = false
  JointType = 0 (Fixed)
  LengthMax = 0
  LengthMin = 0
  Offset2 = pos=(0,0,3) rot=(0,0,-1;3.14159rad)
  Placement1 = pos=(4,-4,4) rot=(-0.57735,-0.57735,0.57735;4.18879rad)
  Placement2 = pos=(-10,10,0) rot=(-0.57735,0.57735,0.57735;2.0944rad)
  Reference1 = -> Assembly [corner_mount006.Body009.Edge48,corner_mount006.Body009.Vertex36]
  Reference2 = -> Assembly [frame._020_150mm_v2.Edge119,frame._020_150mm_v2.Edge119]
FEATURE [App::FeaturePython] Joint009  label="Fixed009"  # Assembly joint (typed FeaturePython)
  Activated = true
  AngleMax = 0
  AngleMin = 0
  Detach1 = false
  Detach2 = false
  Distance = 0
  Distance2 = 0
  EnableAngleMax = false
  EnableAngleMin = false
  EnableLengthMax = false
  EnableLengthMin = false
  JointType = 0 (Fixed)
  LengthMax = 0
  LengthMin = 0
  Offset2 = pos=(0,0,-3) rot=(0,0,1;3.14159rad)
  Placement1 = pos=(24,-4,4) rot=(0.707107,0,0.707107;3.14159rad)
  Placement2 = pos=(-10,10,150) rot=(0,-1,0;4.71239rad)
  Reference1 = -> Assembly [corner_mount004.Body007.Edge46,corner_mount004.Body007.Edge46]
  Reference2 = -> Assembly [frame._020_150mm_v008.Edge26,frame._020_150mm_v008.Edge26]
FEATURE [App::Link] Body
  LinkPlacement = pos=(180,-280,24) rot=(0,0,1;1.5708rad)
  LinkedObject = -> <external mechanism/base.FCStd>#Body
  Placement = pos=(180,-280,24) rot=(0,0,1;1.5708rad)
FEATURE [App::FeaturePython] Joint010  label="Fixed010"  # Assembly joint (typed FeaturePython)
  Activated = true
  AngleMax = 0
  AngleMin = 0
  Detach1 = false
  Detach2 = false
  Distance = 0
  Distance2 = 0
  EnableAngleMax = false
  EnableAngleMin = false
  EnableLengthMax = false
  EnableLengthMin = false
  JointType = 0 (Fixed)
  LengthMax = 0
  LengthMin = 0
  Offset1 = pos=(0,1,0) rot=(0,0,1;0rad)
  Offset2 = pos=(0,0,0) rot=(0,0,1;3.14159rad)
  Placement1 = pos=(1,95,-4) rot=(-0.57735,-0.57735,0.57735;4.18879rad)
  Placement2 = pos=(-10,-9,75) rot=(1,0,0;3.14159rad)
  Reference1 = -> Assembly [Body.Edge78,Body.Edge78]
  Reference2 = -> Assembly [frame._020_150mm_v009.Edge128,frame._020_150mm_v009.Edge128]
FEATURE [App::Link] Body010
  LinkPlacement = pos=(35.84,-161.85,21) rot=(0,0,1;1.5708rad)
  LinkedObject = -> <external mechanism/rod.FCStd>#Body
  Placement = pos=(35.84,-161.85,21) rot=(0,0,1;1.5708rad)
FEATURE [App::FeaturePython] Joint011  label="Fixed011"  # Assembly joint (typed FeaturePython)
  Activated = true
  AngleMax = 0
  AngleMin = 0
  Detach1 = false
  Detach2 = false
  Distance = 0
  Distance2 = 0
  EnableAngleMax = false
  EnableAngleMin = false
  EnableLengthMax = false
  EnableLengthMin = false
  JointType = 0 (Fixed)
  LengthMax = 0
  LengthMin = 0
  Placement2 = pos=(118.15,144.16,-3) rot=(0,0,1;0rad)
  Reference1 = -> Assembly [Body010.Face2,Body010.Face2]
  Reference2 = -> Assembly [Body.Face34,Body.Face34]
FEATURE [App::Link] Body011
  LinkPlacement = pos=(35.84,-220.15,150) rot=(0.707107,0.707107,0;3.14159rad)
  LinkedObject = -> <external mechanism/rod.FCStd>#Body
  Placement = pos=(35.84,-220.15,150) rot=(0.707107,0.707107,0;3.14159rad)
FEATURE [App::FeaturePython] Joint012  label="Fixed012"  # Assembly joint (typed FeaturePython)
  Activated = true
  AngleMax = 0
  AngleMin = 0
  Detach1 = false
  Detach2 = false
  Distance = 0
  Distance2 = 0
  EnableAngleMax = false
  EnableAngleMin = false
  EnableLengthMax = false
  EnableLengthMin = false
  JointType = 0 (Fixed)
  LengthMax = 0
  LengthMin = 0
  Placement1 = pos=(0,0,129) rot=(0,0,1;0rad)
  Placement2 = pos=(59.85,144.16,-3) rot=(0,0,1;0rad)
  Reference1 = -> Assembly [Body011.Face3,Body011.Face3]
  Reference2 = -> Assembly [Body.Face33,Body.Edge1]
FEATURE [App::Link] Body012
  LinkPlacement = pos=(35.84,-191,118.99) rot=(0,0,-1;1.5708rad)
  LinkedObject = -> <external mechanism/head.FCStd>#Body
  Placement = pos=(35.84,-191,118.99) rot=(0,0,-1;1.5708rad)
FEATURE [App::FeaturePython] Joint013  label="Slider013"  # Assembly joint (typed FeaturePython)
  Activated = true
  AngleMax = 0
  AngleMin = 0
  Detach1 = false
  Detach2 = false
  Distance = 0
  Distance2 = 0
  EnableAngleMax = false
  EnableAngleMin = false
  EnableLengthMax = true
  EnableLengthMin = true
  JointType = 3 (Slider)
  LengthMax = 10
  LengthMin = -23
  Offset2 = pos=(0,0,29) rot=(0,0,1;3.14159rad)
  Placement1 = pos=(0,0,-29) rot=(0,0,1;0rad)
  Placement2 = pos=(89,144.16,52) rot=(0,0,1;3.14159rad)
  Reference1 = -> Assembly [Body012.Edge71,Body012.Edge71]
  Reference2 = -> Assembly [Body.Edge16,Body.Edge16]
FEATURE [App::Link] Body013
  LinkPlacement = pos=(-10,-233.5,150) rot=(0.707107,0.707107,0;3.14159rad)
  LinkedObject = -> <external mechanism/top.FCStd>#Body
  Placement = pos=(-10,-233.5,150) rot=(0.707107,0.707107,0;3.14159rad)
FEATURE [App::FeaturePython] Joint014  label="Fixed013"  # Assembly joint (typed FeaturePython)
  Activated = true
  AngleMax = 0
  AngleMin = 0
  Detach1 = false
  Detach2 = false
  Distance = 0
  Distance2 = 0
  EnableAngleMax = false
  EnableAngleMin = false
  EnableLengthMax = false
  EnableLengthMin = false
  JointType = 0 (Fixed)
  LengthMax = 0
  LengthMin = 0
  Offset1 = pos=(56,0,-6) rot=(0,0,1;0rad)
  Offset2 = pos=(0,0,0) rot=(0,0,1;1.5708rad)
  Placement1 = pos=(98.5,14,10) rot=(-1,0,0;1.5708rad)
  Placement2 = pos=(4,0,125) rot=(-0.707107,0,-0.707107;3.14159rad)
  Reference1 = -> Assembly [Body013.Face15,Body013.Face15]
  Reference2 = -> Assembly [frame._020_250mm_v003.Face44,frame._020_250mm_v003.Face44]
FEATURE [App::Link] Body014
  LinkPlacement = pos=(-11.25,9.00002,-3.8147e-06) rot=(0,0,-1;1.5708rad)
  LinkedObject = -> <external mechanism/stm_mount.FCStd>#Body
  Placement = pos=(-11.25,9.00002,-3.8147e-06) rot=(0,0,-1;1.5708rad)
FEATURE [App::FeaturePython] Joint015  label="Fixed014"  # Assembly joint (typed FeaturePython)
  Activated = true
  AngleMax = 0
  AngleMin = 0
  Detach1 = false
  Detach2 = false
  Distance = 0
  Distance2 = 0
  EnableAngleMax = false
  EnableAngleMin = false
  EnableLengthMax = false
  EnableLengthMin = false
  JointType = 0 (Fixed)
  LengthMax = 0
  LengthMin = 0
  Offset2 = pos=(0,0,0) rot=(0,0,1;3.14159rad)
  Placement1 = pos=(2.13e-14,96.25,0) rot=(-0.57735,-0.57735,0.57735;4.18879rad)
  Placement2 = pos=(-10,9,75) rot=(0,0,1;3.14159rad)
  Reference1 = -> Assembly [Body014.Edge10,Body014.Edge10]
  Reference2 = -> Assembly [frame._020_150mm_v005.Edge133,frame._020_150mm_v005.Edge133]
FEATURE [App::Link] Body015
  LinkPlacement = pos=(-5.00002,-233.5,132) rot=(0.707107,0.707107,0;3.14159rad)
  LinkedObject = -> <external mechanism/profile_cover.FCStd>#Body
  Placement = pos=(-5.00002,-233.5,132) rot=(0.707107,0.707107,0;3.14159rad)
FEATURE [App::FeaturePython] Joint016  label="Fixed015"  # Assembly joint (typed FeaturePython)
  Activated = true
  AngleMax = 0
  AngleMin = 0
  Detach1 = false
  Detach2 = false
  Distance = 0
  Distance2 = 0
  EnableAngleMax = false
  EnableAngleMin = false
  EnableLengthMax = false
  EnableLengthMin = false
  JointType = 0 (Fixed)
  LengthMax = 0
  LengthMin = 0
  Offset1 = pos=(-56,0,0) rot=(0,0,1;0rad)
  Offset2 = pos=(0,0,0) rot=(0,0,1;3.14159rad)
  Placement1 = pos=(98.5,9,1) rot=(0,0.382683,-0.92388;3.14159rad)
  Placement2 = pos=(4,9,125) rot=(-0.678598,0.281085,0.678598;2.59356rad)
  Reference1 = -> Assembly [Body015.Face5,Body015.Face5]
  Reference2 = -> Assembly [frame._020_250mm_v003.Face11,frame._020_250mm_v003.Face11]
FEATURE [App::Link] Body016
  LinkPlacement = pos=(94.59,-188.35,81.3395) rot=(0,-0.707107,0.707107;3.14159rad)
  LinkedObject = -> <external mechanism/funnel.FCStd>#Body
  Placement = pos=(94.59,-188.35,81.3395) rot=(0,-0.707107,0.707107;3.14159rad)
FEATURE [App::FeaturePython] Joint017  label="Fixed016"  # Assembly joint (typed FeaturePython)
  Activated = true
  AngleMax = 0
  AngleMin = 0
  Detach1 = false
  Detach2 = false
  Distance = 0
  Distance2 = 0
  EnableAngleMax = false
  EnableAngleMin = false
  EnableLengthMax = false
  EnableLengthMin = false
  JointType = 0 (Fixed)
  LengthMax = 0
  LengthMin = 0
  Offset1 = pos=(29.5,0,0) rot=(0,0,1;0rad)
  Offset2 = pos=(0,0,-15) rot=(0,0,1;1.5708rad)
  Placement1 = pos=(33,3,15) rot=(0,0,1;0rad)
  Placement2 = pos=(12.35,25.75,-40.65) rot=(-0.57735,0.57735,0.57735;4.18879rad)
  Reference1 = -> Assembly [Body016.Edge29,Body016.Edge29]
  Reference2 = -> Assembly [Body012.Edge80,Body012.Vertex13]
FEATURE [App::Link] Body017
  LinkPlacement = pos=(55.99,-188.35,104.34) rot=(1,0,0;1.5708rad)
  LinkedObject = -> <external mechanism/bearing_holder.FCStd>#Body
  Placement = pos=(55.99,-188.35,104.34) rot=(1,0,0;1.5708rad)
FEATURE [App::FeaturePython] Joint018  label="Fixed017"  # Assembly joint (typed FeaturePython)
  Activated = true
  AngleMax = 0
  AngleMin = 0
  Detach1 = false
  Detach2 = false
  Distance = 0
  Distance2 = 0
  EnableAngleMax = false
  EnableAngleMin = false
  EnableLengthMax = false
  EnableLengthMin = false
  JointType = 0 (Fixed)
  LengthMax = 0
  LengthMin = 0
  Placement1 = pos=(35,5,0) rot=(0,0,1;0rad)
  Placement2 = pos=(-2.65,55.15,-9.65) rot=(0.57735,0.57735,0.57735;2.0944rad)
  Reference1 = -> Assembly [Body017.Edge17,Body017.Edge17]
  Reference2 = -> Assembly [Body012.Face13,Body012.Edge1]
FEATURE [App::Link] Body018
  LinkPlacement = pos=(184,10,154) rot=(0,0,1;1.5708rad)
  LinkedObject = -> <external Screen/Screen_v3.FCStd>#Body
  Placement = pos=(184,10,154) rot=(0,0,1;1.5708rad)
FEATURE [App::FeaturePython] Joint019  label="Fixed018"  # Assembly joint (typed FeaturePython)
  Activated = true
  AngleMax = 0
  AngleMin = 0
  Detach1 = false
  Detach2 = false
  Distance = 0
  Distance2 = 0
  EnableAngleMax = false
  EnableAngleMin = false
  EnableLengthMax = false
  EnableLengthMin = false
  JointType = 0 (Fixed)
  LengthMax = 0
  LengthMin = 0
  Offset1 = pos=(0,-6,0) rot=(0,0,1;0rad)
  Placement1 = pos=(-10,10,-4) rot=(-0.707107,0,0.707107;3.14159rad)
  Placement2 = pos=(4,0,150) rot=(-0.57735,-0.57735,0.57735;4.18879rad)
  Reference1 = -> Assembly [Body018.?Edge20,Body018.?Edge20]
  Reference2 = -> Assembly [frame._020_150mm_v004.Edge9,frame._020_150mm_v004.Edge9]
FEATURE [Assembly::JointGroup] Joints
  Group = -> [GroundedJoint,Joint,Joint001,Joint002,Joint003,Joint004,Joint005,Joint007,Joint008,Joint009,Joint010,Joint011,Joint012,Joint013,Joint014,Joint015,Joint016,Joint017,Joint018,Joint019]
FEATURE [Assembly::AssemblyObject] Assembly  label="tip-etcher"
  Group = -> [Joints,psu_mount,frame,l_mount,corner_mount,l_mount001,corner_mount002,corner_mount003,corner_mount004,corner_mount005,GroundedJoint,Joint,Joint001,Joint002,Joint003,Joint004,Joint005,Joint007,corner_mount006,Joint008,Joint009,Body,Joint010,Body010,Joint011,Body011,Joint012,Body012,Joint013,Body013,Joint014,Body014,Joint015,Body015,Joint016,Body016,Joint017,Body017,Joint018,Body018,Joint019]
  Origin = -> Origin
  Type = Assembly

RESOLVED EXTERNAL PARTS (link-assembly join: the EXTERNAL_REF files above that resolve inside this repo's crawl, each included once):
---- part frame/L-mount.FCStd = doc fcstd_c02f1ebd9fad ----
FCSTD DOCUMENT  (FreeCAD 1.0R39285 (Git))
Label: L-mount
License: All rights reserved
objects: App::Link×7, App::FeaturePython×7, Sketcher::SketchObject×4, PartDesign::Pad×4, PartDesign::Chamfer×2, PartDesign::Body×1, Part::FeaturePython×1, Assembly::JointGroup×1, Assembly::AssemblyObject×1
note: 28 computed .brp shape members not serialized (recipe doc carries the construction recipe); baked Part::Feature solids carry a one-line shape summary decoded from their .brp

FEATURE [Sketcher::SketchObject] Sketch
  ArcFitTolerance = 1e-06
  AttachmentSupport = -> [XY_Plane]
  FullyConstrained = true
  MakeInternals = false
  MapMode = 5
  sketch-geometry (7):
    g0: LineSegment StartX=0 StartY=0 StartZ=0 EndX=28 EndY=0 EndZ=0
    g1: LineSegment StartX=28 StartY=0 StartZ=0 EndX=28 EndY=44 EndZ=0
    g2: LineSegment StartX=28 StartY=44 StartZ=0 EndX=0 EndY=44 EndZ=0
    g3: LineSegment StartX=0 StartY=44 StartZ=0 EndX=0 EndY=0 EndZ=0
    g4: LineSegment [constr] StartX=28 StartY=44 StartZ=0 EndX=14 EndY=44 EndZ=0
    g5: LineSegment [constr] StartX=14 StartY=44 StartZ=0 EndX=14 EndY=34 EndZ=0
    g6: Circle CenterX=14 CenterY=34 CenterZ=0 NormalX=0 NormalY=0 NormalZ=1 AngleXU=0 Radius=2.6
  constraints (18):
    c: Coincident(g0,g1)
    c: Coincident(g1,g2)
    c: Coincident(g2,g3)
    c: Coincident(g3,g0)
    c: Horizontal(g0)
    c: Horizontal(g2)
    c: Vertical(g1)
    c: Vertical(g3)
    c: Distance(g1,g3) = 28
    c: Distance(g0,g2) = 44
    c: Coincident(g0,g-1)
    c: Coincident(g4,g1)
    c: Symmetric(g2,g2,g4)
    c: Distance(g5) = 10
    c: Coincident(g5,g4)
    c: Vertical(g5)
    c: Diameter(g6) = 5.2
    c: Coincident(g6,g5)
FEATURE [PartDesign::Pad] Pad
  Direction = (0,0,1)
  Length = 4
  Length2 = 10
  Profile = -> Sketch
  ReferenceAxis = -> Sketch [N_Axis]
  Refine = true
  Suppressed = false
  Type = 0
FEATURE [Sketcher::SketchObject] Sketch001
  ArcFitTolerance = 1e-06
  AttachmentSupport = -> [Pad]
  FullyConstrained = true
  MakeInternals = false
  MapMode = 5
  Placement = pos=(0,0,0) rot=(1,0,0;1.5708rad)
  sketch-geometry (7):
    g0: LineSegment StartX=0 StartY=0 StartZ=0 EndX=28 EndY=0 EndZ=0
    g1: LineSegment StartX=28 StartY=0 StartZ=0 EndX=28 EndY=44 EndZ=0
    g2: LineSegment StartX=28 StartY=44 StartZ=0 EndX=0 EndY=44 EndZ=0
    g3: LineSegment StartX=0 StartY=44 StartZ=0 EndX=0 EndY=0 EndZ=0
    g4: LineSegment [constr] StartX=28 StartY=44 StartZ=0 EndX=14 EndY=44 EndZ=0
    g5: LineSegment [constr] StartX=14 StartY=44 StartZ=0 EndX=14 EndY=34 EndZ=0
    g6: Circle CenterX=14 CenterY=34 CenterZ=0 NormalX=0 NormalY=0 NormalZ=1 AngleXU=0 Radius=2.6
  constraints (18):
    c: Coincident(g0,g1)
    c: Coincident(g1,g2)
    c: Coincident(g2,g3)
    c: Coincident(g3,g0)
    c: Horizontal(g0)
    c: Horizontal(g2)
    c: Vertical(g1)
    c: Vertical(g3)
    c: Distance(g1,g3) = 28
    c: Distance(g0,g2) = 44
    c: Coincident(g0,g-1)
    c: Coincident(g4,g1)
    c: Symmetric(g2,g2,g4)
    c: Distance(g5) = 10
    c: Coincident(g5,g4)
    c: Vertical(g5)
    c: Diameter(g6) = 5.2
    c: Coincident(g6,g5)
FEATURE [PartDesign::Pad] Pad001
  BaseFeature = -> Pad
  Direction = (0,-1,2e-16)
  Length = 4
  Length2 = 10
  Profile = -> Sketch001
  ReferenceAxis = -> Sketch001 [N_Axis]
  Refine = true
  Reversed = true
  Suppressed = false
  Type = 0
FEATURE [Sketcher::SketchObject] Sketch002
  ArcFitTolerance = 1e-06
  AttachmentSupport = -> [Pad001]
  FullyConstrained = true
  MakeInternals = false
  MapMode = 5
  Placement = pos=(0,0,0) rot=(0.57735,-0.57735,-0.57735;2.0944rad)
  sketch-geometry (11):
    g0: LineSegment StartX=0 StartY=0 StartZ=0 EndX=0 EndY=44 EndZ=0
    g1: LineSegment StartX=0 StartY=44 StartZ=0 EndX=-24 EndY=44 EndZ=0
    g2: LineSegment StartX=0 StartY=0 StartZ=0 EndX=-44 EndY=0 EndZ=0
    g3: LineSegment StartX=-44 StartY=0 StartZ=0 EndX=-44 EndY=24 EndZ=0
    g4: LineSegment StartX=-44 StartY=24 StartZ=0 EndX=-24 EndY=44 EndZ=0
    g5: LineSegment [constr] StartX=-24 StartY=44 StartZ=0 EndX=-14 EndY=44 EndZ=0
    g6: LineSegment [constr] StartX=-14 StartY=44 StartZ=0 EndX=-14 EndY=34 EndZ=0
    g7: Circle CenterX=-14 CenterY=34 CenterZ=0 NormalX=0 NormalY=0 NormalZ=1 AngleXU=0 Radius=2.6
    g8: LineSegment [constr] StartX=-44 StartY=24 StartZ=0 EndX=-44 EndY=14 EndZ=0
    g9: LineSegment [constr] StartX=-44 StartY=14 StartZ=0 EndX=-34 EndY=14 EndZ=0
    g10: Circle CenterX=-34 CenterY=14 CenterZ=0 NormalX=0 NormalY=0 NormalZ=1 AngleXU=0 Radius=2.6
  constraints (30):
    c: Distance(g0) = 44
    c: Coincident(g0,g-1)
    c: PointOnObject(g0,g-2)
    c: Distance(g1) = 24
    c: Coincident(g1,g0)
    c: Horizontal(g1)
    c: Distance(g2) = 44
    c: Coincident(g2,g0)
    c: PointOnObject(g2,g-1)
    c: Distance(g3) = 24
    c: Coincident(g3,g2)
    c: Vertical(g3)
    c: Coincident(g4,g3)
    c: Coincident(g4,g1)
    c: Distance(g5) = 10
    c: Coincident(g5,g1)
    c: PointOnObject(g5,g1)
    c: Distance(g6) = 10
    c: Coincident(g6,g5)
    c: Vertical(g6)
    c: Diameter(g7) = 5.2
    c: Coincident(g7,g6)
    c: Distance(g8) = 10
    c: Coincident(g8,g3)
    c: PointOnObject(g8,g3)
    c: Distance(g9) = 10
    c: Coincident(g9,g8)
    c: Horizontal(g9)
    c: Diameter(g10) = 5.2
    c: Coincident(g10,g9)
FEATURE [PartDesign::Pad] Pad002
  BaseFeature = -> Pad001
  Direction = (-1,0,0)
  Length = 4
  Length2 = 10
  Profile = -> Sketch002
  ReferenceAxis = -> Sketch002 [N_Axis]
  Refine = true
  Reversed = true
  Suppressed = false
  Type = 0
FEATURE [Sketcher::SketchObject] Sketch003
  ArcFitTolerance = 1e-06
  AttachmentSupport = -> [Pad002]
  FullyConstrained = true
  MakeInternals = false
  MapMode = 5
  Placement = pos=(28,0,0) rot=(0.57735,0.57735,0.57735;2.0944rad)
  sketch-geometry (11):
    g0: LineSegment StartX=0 StartY=0 StartZ=0 EndX=0 EndY=44 EndZ=0
    g1: LineSegment StartX=0 StartY=0 StartZ=0 EndX=44 EndY=0 EndZ=0
    g2: LineSegment StartX=0 StartY=44 StartZ=0 EndX=24 EndY=44 EndZ=0
    g3: LineSegment StartX=44 StartY=0 StartZ=0 EndX=44 EndY=24 EndZ=0
    g4: LineSegment StartX=24 StartY=44 StartZ=0 EndX=44 EndY=24 EndZ=0
    g5: LineSegment [constr] StartX=44 StartY=24 StartZ=0 EndX=44 EndY=14 EndZ=0
    g6: LineSegment [constr] StartX=44 StartY=14 StartZ=0 EndX=34 EndY=14 EndZ=0
    g7: Circle CenterX=34 CenterY=14 CenterZ=0 NormalX=0 NormalY=0 NormalZ=1 AngleXU=0 Radius=2.6
    g8: LineSegment [constr] StartX=24 StartY=44 StartZ=0 EndX=14 EndY=44 EndZ=0
    g9: LineSegment [constr] StartX=14 StartY=44 StartZ=0 EndX=14 EndY=34 EndZ=0
    g10: Circle CenterX=14 CenterY=34 CenterZ=0 NormalX=0 NormalY=0 NormalZ=1 AngleXU=0 Radius=2.6
  constraints (30):
    c: Distance(g0) = 44
    c: Coincident(g0,g-1)
    c: PointOnObject(g0,g-2)
    c: Distance(g1) = 44
    c: Coincident(g1,g0)
    c: PointOnObject(g1,g-1)
    c: Distance(g2) = 24
    c: Coincident(g2,g0)
    c: Horizontal(g2)
    c: Distance(g3) = 24
    c: Coincident(g3,g1)
    c: Vertical(g3)
    c: Coincident(g4,g2)
    c: Coincident(g4,g3)
    c: Distance(g5) = 10
    c: Coincident(g5,g3)
    c: PointOnObject(g5,g3)
    c: Distance(g6) = 10
    c: Coincident(g6,g5)
    c: Horizontal(g6)
    c: Diameter(g7) = 5.2
    c: Coincident(g7,g6)
    c: Distance(g8) = 10
    c: Coincident(g8,g2)
    c: PointOnObject(g8,g2)
    c: Distance(g9) = 10
    c: Coincident(g9,g8)
    c: Vertical(g9)
    c: Diameter(g10) = 5.2
    c: Coincident(g10,g9)
FEATURE [PartDesign::Pad] Pad003
  BaseFeature = -> Pad002
  Direction = (1,0,0)
  Length = 4
  Length2 = 10
  Profile = -> Sketch003
  ReferenceAxis = -> Sketch003 [N_Axis]
  Refine = true
  Reversed = true
  Suppressed = false
  Type = 0
FEATURE [PartDesign::Chamfer] Chamfer
  Angle = 45
  Base = -> Pad003 [Edge1,Edge46,Edge45,Edge5,Edge42]
  BaseFeature = -> Pad003
  ChamferType = 0
  FlipDirection = false
  Refine = true
  Size = 3
  Size2 = 1
  SupportTransform = false
  Suppressed = false
  UseAllEdges = false
FEATURE [PartDesign::Chamfer] Chamfer001
  Angle = 45
  Base = -> Chamfer [Edge19,Edge26,Edge10,Edge16]
  BaseFeature = -> Chamfer
  ChamferType = 0
  FlipDirection = false
  Refine = true
  Size = 2
  Size2 = 1
  SupportTransform = false
  Suppressed = false
  UseAllEdges = false
FEATURE [PartDesign::Body] Body
  AllowCompound = false
  Group = -> [Sketch,Pad,Sketch001,Pad001,Sketch002,Pad002,Sketch003,Pad003,Chamfer,Chamfer001]
  Origin = -> Origin
  Tip = -> Chamfer001
FEATURE [App::Link] Body001
  LinkedObject = -> Body
FEATURE [Part::FeaturePython] Screw  label="M5x10-Screw"  # WARN: FeaturePython — macro-defined, semantics opaque (R4)
  Diameter = 3
  Invert = false
  LeftHanded = false
  Length = 1
  LengthCustom = 10
  MatchOuter = false
  OffsetAngle = 0
  Placement = pos=(66,0,0) rot=(0,0,1;0rad)
  Thread = false
  Type = 85
FEATURE [App::Link] M5x10_Screw  label="M5x10-Screw001"
  LinkPlacement = pos=(14,34,0) rot=(1,0,0;3.14159rad)
  LinkedObject = -> Screw
  Placement = pos=(14,34,0) rot=(1,0,0;3.14159rad)
FEATURE [App::Link] M5x10_Screw001  label="M5x10-Screw002"
  LinkPlacement = pos=(28.2,34,14) rot=(0.57735,0.57735,0.57735;2.0944rad)
  LinkedObject = -> Screw
  Placement = pos=(28.2,34,14) rot=(0.57735,0.57735,0.57735;2.0944rad)
FEATURE [App::Link] M5x10_Screw002  label="M5x10-Screw003"
  LinkPlacement = pos=(14,0,34) rot=(1,0,0;1.5708rad)
  LinkedObject = -> Screw
  Placement = pos=(14,0,34) rot=(1,0,0;1.5708rad)
FEATURE [App::Link] M5x10_Screw003  label="M5x10-Screw004"
  LinkPlacement = pos=(-0.2,34,14) rot=(0.57735,-0.57735,-0.57735;2.0944rad)
  LinkedObject = -> Screw
  Placement = pos=(-0.2,34,14) rot=(0.57735,-0.57735,-0.57735;2.0944rad)
FEATURE [App::Link] M5x10_Screw004  label="M5x10-Screw005"
  LinkPlacement = pos=(-0.2,14,34) rot=(0.57735,-0.57735,-0.57735;2.0944rad)
  LinkedObject = -> Screw
  Placement = pos=(-0.2,14,34) rot=(0.57735,-0.57735,-0.57735;2.0944rad)
FEATURE [App::Link] M5x10_Screw005  label="M5x10-Screw006"
  LinkPlacement = pos=(28.2,14,34) rot=(0.57735,0.57735,0.57735;2.0944rad)
  LinkedObject = -> Screw
  Placement = pos=(28.2,14,34) rot=(0.57735,0.57735,0.57735;2.0944rad)
FEATURE [App::FeaturePython] GroundedJoint  # Assembly grounded joint (typed FeaturePython)
  ObjectToGround = -> Body001
FEATURE [App::FeaturePython] Joint  label="Fixed"  # Assembly joint (typed FeaturePython)
  Activated = true
  AngleMax = 0
  AngleMin = 0
  Detach1 = false
  Detach2 = false
  Distance = 0
  Distance2 = 0
  EnableAngleMax = false
  EnableAngleMin = false
  EnableLengthMax = false
  EnableLengthMin = false
  JointType = 0 (Fixed)
  LengthMax = 0
  LengthMin = 0
  Placement1 = pos=(0,0,-0.2) rot=(0,0,1;0rad)
  Placement2 = pos=(28,34,14) rot=(0.57735,0.57735,0.57735;2.0944rad)
  Reference1 = -> Assembly [M5x10_Screw001.Edge13,M5x10_Screw001.Edge13]
  Reference2 = -> Assembly [Body001.Edge46,Body001.Edge46]
FEATURE [App::FeaturePython] Joint001  label="Fixed001"  # Assembly joint (typed FeaturePython)
  Activated = true
  AngleMax = 0
  AngleMin = 0
  Detach1 = false
  Detach2 = false
  Distance = 0
  Distance2 = 0
  EnableAngleMax = false
  EnableAngleMin = false
  EnableLengthMax = false
  EnableLengthMin = false
  JointType = 0 (Fixed)
  LengthMax = 0
  LengthMin = 0
  Placement1 = pos=(0,0,-0.2) rot=(0,0,1;0rad)
  Placement2 = pos=(28,14,34) rot=(0.57735,0.57735,0.57735;2.0944rad)
  Reference1 = -> Assembly [M5x10_Screw005.Edge13,M5x10_Screw005.Edge13]
  Reference2 = -> Assembly [Body001.Edge47,Body001.Edge47]
FEATURE [App::FeaturePython] Joint002  label="Fixed002"  # Assembly joint (typed FeaturePython)
  Activated = true
  AngleMax = 0
  AngleMin = 0
  Detach1 = false
  Detach2 = false
  Distance = 0
  Distance2 = 0
  EnableAngleMax = false
  EnableAngleMin = false
  EnableLengthMax = false
  EnableLengthMin = false
  JointType = 0 (Fixed)
  LengthMax = 0
  LengthMin = 0
  Placement2 = pos=(14,34,0) rot=(0,0,1;0rad)
  Reference1 = -> Assembly [M5x10_Screw.Edge5,M5x10_Screw.Edge5]
  Reference2 = -> Assembly [Body001.Edge67,Body001.Edge67]
FEATURE [App::FeaturePython] Joint003  label="Fixed003"  # Assembly joint (typed FeaturePython)
  Activated = true
  AngleMax = 0
  AngleMin = 0
  Detach1 = false
  Detach2 = false
  Distance = 0
  Distance2 = 0
  EnableAngleMax = false
  EnableAngleMin = false
  EnableLengthMax = false
  EnableLengthMin = false
  JointType = 0 (Fixed)
  LengthMax = 0
  LengthMin = 0
  Placement2 = pos=(14,0,34) rot=(1,0,0;1.5708rad)
  Reference1 = -> Assembly [M5x10_Screw002.Edge5,M5x10_Screw002.Edge5]
  Reference2 = -> Assembly [Body001.Edge59,Body001.Edge59]
FEATURE [App::FeaturePython] Joint004  label="Fixed004"  # Assembly joint (typed FeaturePython)
  Activated = true
  AngleMax = 0
  AngleMin = 0
  Detach1 = false
  Detach2 = false
  Distance = 0
  Distance2 = 0
  EnableAngleMax = false
  EnableAngleMin = false
  EnableLengthMax = false
  EnableLengthMin = false
  JointType = 0 (Fixed)
  LengthMax = 0
  LengthMin = 0
  Placement1 = pos=(0,0,-0.2) rot=(0,0,1;0rad)
  Placement2 = pos=(0,34,14) rot=(-0.57735,0.57735,0.57735;4.18879rad)
  Reference1 = -> Assembly [M5x10_Screw003.Edge13,M5x10_Screw003.Edge13]
  Reference2 = -> Assembly [Body001.Edge8,Body001.Edge8]
FEATURE [App::FeaturePython] Joint005  label="Fixed005"  # Assembly joint (typed FeaturePython)
  Activated = true
  AngleMax = 0
  AngleMin = 0
  Detach1 = false
  Detach2 = false
  Distance = 0
  Distance2 = 0
  EnableAngleMax = false
  EnableAngleMin = false
  EnableLengthMax = false
  EnableLengthMin = false
  JointType = 0 (Fixed)
  LengthMax = 0
  LengthMin = 0
  Placement1 = pos=(0,0,-0.2) rot=(0,0,1;0rad)
  Placement2 = pos=(0,14,34) rot=(-0.57735,0.57735,0.57735;4.18879rad)
  Reference1 = -> Assembly [M5x10_Screw004.Edge13,M5x10_Screw004.Edge13]
  Reference2 = -> Assembly [Body001.Edge9,Body001.Edge9]
FEATURE [Assembly::JointGroup] Joints
  Group = -> [GroundedJoint,Joint,Joint001,Joint002,Joint003,Joint004,Joint005]
FEATURE [Assembly::AssemblyObject] Assembly  label="l-mount"
  Group = -> [Joints,Body001,M5x10_Screw,M5x10_Screw001,M5x10_Screw002,M5x10_Screw003,M5x10_Screw004,M5x10_Screw005,GroundedJoint,Joint,Joint001,Joint002,Joint003,Joint004,Joint005]
  Origin = -> Origin001
  Type = Assembly
---- part frame/assembly-frame.FCStd = doc fcstd_7c2358bc09b8 ----
FCSTD DOCUMENT  (FreeCAD 1.0R39285 (Git))
Label: assembly-frame
License: All rights reserved
objects: App::Link×11, App::FeaturePython×11, Part::Feature×2, Assembly::JointGroup×1, Assembly::AssemblyObject×1
note: 2 computed .brp shape members not serialized (recipe doc carries the construction recipe); baked Part::Feature solids carry a one-line shape summary decoded from their .brp

FEATURE [Part::Feature] Part__Feature  label="2020_150mm v2"
  shape: bbox 20 x 20 x 150 mm, 51 faces (baked)
FEATURE [App::Link] _020_150mm_v2  label="2020_150mm_001"
  LinkedObject = -> Part__Feature
FEATURE [App::Link] _020_150mm_v003  label="2020_150mm_002"
  LinkPlacement = pos=(160,1.8e-15,140) rot=(0,-1,0;1.5708rad)
  LinkedObject = -> Part__Feature
  Placement = pos=(160,1.8e-15,140) rot=(0,-1,0;1.5708rad)
FEATURE [App::FeaturePython] GroundedJoint  # Assembly grounded joint (typed FeaturePython)
  ObjectToGround = -> _020_150mm_v2
FEATURE [App::FeaturePython] Joint  label="Fixed"  # Assembly joint (typed FeaturePython)
  Activated = true
  AngleMax = 0
  AngleMin = 0
  Detach1 = false
  Detach2 = false
  Distance = 0
  Distance2 = 0
  EnableAngleMax = false
  EnableAngleMin = false
  EnableLengthMax = false
  EnableLengthMin = false
  JointType = 0 (Fixed)
  LengthMax = 0
  LengthMin = 0
  Offset2 = pos=(0,0,0) rot=(0,0,1;1.5708rad)
  Placement1 = pos=(10,-7,150) rot=(-0.57735,-0.57735,0.57735;4.18879rad)
  Placement2 = pos=(10,-7,150) rot=(-1,0,0;4.71239rad)
  Reference1 = -> Assembly [_020_150mm_v003.Edge4,_020_150mm_v003.Edge4]
  Reference2 = -> Assembly [_020_150mm_v2.Edge4,_020_150mm_v2.Edge4]
FEATURE [App::Link] _020_150mm_v004  label="2020_150mm_003"
  LinkPlacement = pos=(170,3.64e-14,-2.49e-14) rot=(0,0,1;0rad)
  LinkedObject = -> Part__Feature
  Placement = pos=(170,3.64e-14,-2.49e-14) rot=(0,0,1;0rad)
FEATURE [App::FeaturePython] Joint001  label="Fixed001"  # Assembly joint (typed FeaturePython)
  Activated = true
  AngleMax = 0
  AngleMin = 0
  Detach1 = false
  Detach2 = false
  Distance = 0
  Distance2 = 0
  EnableAngleMax = false
  EnableAngleMin = false
  EnableLengthMax = false
  EnableLengthMin = false
  JointType = 0 (Fixed)
  LengthMax = 0
  LengthMin = 0
  Offset2 = pos=(0,0,0) rot=(0,0,1;1.5708rad)
  Placement1 = pos=(-10,-7,150) rot=(0.57735,0.57735,0.57735;4.18879rad)
  Placement2 = pos=(10,-7,0) rot=(-1,0,0;4.71239rad)
  Reference1 = -> Assembly [_020_150mm_v004.Edge38,_020_150mm_v004.Edge38]
  Reference2 = -> Assembly [_020_150mm_v003.Edge92,_020_150mm_v003.Edge92]
FEATURE [App::Link] _020_150mm_v005  label="2020_150mm_004"
  LinkPlacement = pos=(160,2.7e-15,10) rot=(0,1,0;4.71239rad)
  LinkedObject = -> Part__Feature
  Placement = pos=(160,2.7e-15,10) rot=(0,1,0;4.71239rad)
FEATURE [App::FeaturePython] Joint002  label="Fixed002"  # Assembly joint (typed FeaturePython)
  Activated = true
  AngleMax = 0
  AngleMin = 0
  Detach1 = false
  Detach2 = false
  Distance = 0
  Distance2 = 0
  EnableAngleMax = false
  EnableAngleMin = false
  EnableLengthMax = false
  EnableLengthMin = false
  JointType = 0 (Fixed)
  LengthMax = 0
  LengthMin = 0
  Offset2 = pos=(0,0,0) rot=(0,0,-1;1.5708rad)
  Placement1 = pos=(-10,-7,150) rot=(0.57735,0.57735,0.57735;4.18879rad)
  Placement2 = pos=(10,-7,0) rot=(0,-0.707107,0.707107;3.14159rad)
  Reference1 = -> Assembly [_020_150mm_v005.Edge38,_020_150mm_v005.Edge38]
  Reference2 = -> Assembly [_020_150mm_v2.Edge92,_020_150mm_v2.Edge92]
FEATURE [Part::Feature] Part__Feature001  label="2020_250mm v2"
  shape: bbox 20 x 20 x 250 mm, 51 faces (baked)
FEATURE [App::Link] _020_250mm_v2  label="2020_250mm_001"
  LinkPlacement = pos=(-1.101e-13,-260,10) rot=(-1,0,0;1.5708rad)
  LinkedObject = -> Part__Feature001
  Placement = pos=(-1.101e-13,-260,10) rot=(-1,0,0;1.5708rad)
FEATURE [App::FeaturePython] Joint003  label="Fixed003"  # Assembly joint (typed FeaturePython)
  Activated = true
  AngleMax = 0
  AngleMin = 0
  Detach1 = false
  Detach2 = false
  Distance = 0
  Distance2 = 0
  EnableAngleMax = false
  EnableAngleMin = false
  EnableLengthMax = false
  EnableLengthMin = false
  JointType = 0 (Fixed)
  LengthMax = 0
  LengthMin = 0
  Offset2 = pos=(0,0,-2) rot=(0,0,1;1.5708rad)
  Placement1 = pos=(9,10,250) rot=(-0.707107,0,0.707107;3.14159rad)
  Placement2 = pos=(9,-10,0) rot=(-0.57735,0.57735,0.57735;4.18879rad)
  Reference1 = -> Assembly [_020_250mm_v2.Edge16,_020_250mm_v2.Vertex16]
  Reference2 = -> Assembly [_020_150mm_v2.Edge96,_020_150mm_v2.Edge96]
FEATURE [App::Link] _020_250mm_v003  label="2020_250mm_002"
  LinkPlacement = pos=(1.11e-13,-260,140) rot=(1,0,0;4.71239rad)
  LinkedObject = -> Part__Feature001
  Placement = pos=(1.11e-13,-260,140) rot=(1,0,0;4.71239rad)
FEATURE [App::Link] _020_250mm_v004  label="2020_250mm_003"
  LinkPlacement = pos=(170,-260,10) rot=(-1,0,0;1.5708rad)
  LinkedObject = -> Part__Feature001
  Placement = pos=(170,-260,10) rot=(-1,0,0;1.5708rad)
FEATURE [App::FeaturePython] Joint005  label="Fixed005"  # Assembly joint (typed FeaturePython)
  Activated = true
  AngleMax = 0
  AngleMin = 0
  Detach1 = false
  Detach2 = false
  Distance = 0
  Distance2 = 0
  EnableAngleMax = false
  EnableAngleMin = false
  EnableLengthMax = false
  EnableLengthMin = false
  JointType = 0 (Fixed)
  LengthMax = 0
  LengthMin = 0
  Offset2 = pos=(0,0,0) rot=(0,0,1;1.5708rad)
  Placement1 = pos=(-7,10,250) rot=(-0.707107,0,0.707107;3.14159rad)
  Placement2 = pos=(-7,-10,0) rot=(-0.57735,0.57735,0.57735;4.18879rad)
  Reference1 = -> Assembly [_020_250mm_v004.Edge26,_020_250mm_v004.Edge26]
  Reference2 = -> Assembly [_020_150mm_v004.Edge107,_020_150mm_v004.Edge107]
FEATURE [App::Link] _020_150mm_v006  label="2020_150mm_005"
  LinkPlacement = pos=(1.814e-13,-270,7.13e-14) rot=(0,0,1;0rad)
  LinkedObject = -> Part__Feature
  Placement = pos=(1.814e-13,-270,7.13e-14) rot=(0,0,1;0rad)
FEATURE [App::FeaturePython] Joint006  label="Fixed006"  # Assembly joint (typed FeaturePython)
  Activated = true
  AngleMax = 0
  AngleMin = 0
  Detach1 = false
  Detach2 = false
  Distance = 0
  Distance2 = 0
  EnableAngleMax = false
  EnableAngleMin = false
  EnableLengthMax = false
  EnableLengthMin = false
  JointType = 0 (Fixed)
  LengthMax = 0
  LengthMin = 0
  Offset2 = pos=(0,0,0) rot=(0,0,1;1.5708rad)
  Placement1 = pos=(-7,10,150) rot=(0.707107,0,0.707107;3.14159rad)
  Placement2 = pos=(-7,-10,0) rot=(-0.57735,0.57735,0.57735;4.18879rad)
  Reference1 = -> Assembly [_020_150mm_v006.Edge26,_020_150mm_v006.Edge26]
  Reference2 = -> Assembly [_020_250mm_v003.Edge63,_020_250mm_v003.Edge63]
FEATURE [App::Link] _020_150mm_v007  label="2020_150mm_006"
  LinkPlacement = pos=(10,-270,140) rot=(0,1,0;1.5708rad)
  LinkedObject = -> Part__Feature
  Placement = pos=(10,-270,140) rot=(0,1,0;1.5708rad)
FEATURE [App::Link] _020_150mm_v008  label="2020_150mm_007"
  LinkPlacement = pos=(170,-270,150) rot=(1,0,0;3.14159rad)
  LinkedObject = -> Part__Feature
  Placement = pos=(170,-270,150) rot=(1,0,0;3.14159rad)
FEATURE [App::Link] _020_150mm_v009  label="2020_150mm_008"
  LinkPlacement = pos=(10,-270,10) rot=(0,1,0;1.5708rad)
  LinkedObject = -> Part__Feature
  Placement = pos=(10,-270,10) rot=(0,1,0;1.5708rad)
FEATURE [App::FeaturePython] Joint010  label="Fixed010"  # Assembly joint (typed FeaturePython)
  Activated = true
  AngleMax = 0
  AngleMin = 0
  Detach1 = false
  Detach2 = false
  Distance = 0
  Distance2 = 0
  EnableAngleMax = false
  EnableAngleMin = false
  EnableLengthMax = false
  EnableLengthMin = false
  JointType = 0 (Fixed)
  LengthMax = 0
  LengthMin = 0
  Offset2 = pos=(0,0,0) rot=(0,0,-1;1.5708rad)
  Placement1 = pos=(7,-10,250) rot=(0.707107,0,0.707107;3.14159rad)
  Placement2 = pos=(7,-10,150) rot=(-0.57735,-0.57735,0.57735;2.0944rad)
  Reference1 = -> Assembly [_020_250mm_v003.Edge2,_020_250mm_v003.Edge2]
  Reference2 = -> Assembly [_020_150mm_v2.Edge2,_020_150mm_v2.Edge2]
FEATURE [App::FeaturePython] Joint011  label="Fixed011"  # Assembly joint (typed FeaturePython)
  Activated = true
  AngleMax = 0
  AngleMin = 0
  Detach1 = false
  Detach2 = false
  Distance = 0
  Distance2 = 0
  EnableAngleMax = false
  EnableAngleMin = false
  EnableLengthMax = false
  EnableLengthMin = false
  JointType = 0 (Fixed)
  LengthMax = 0
  LengthMin = 0
  Offset2 = pos=(0,0,0) rot=(0,0,1;1.5708rad)
  Placement1 = pos=(-10,7,1.8e-15) rot=(0.57735,0.57735,0.57735;4.18879rad)
  Placement2 = pos=(10,7,150) rot=(-1,0,0;4.71239rad)
  Reference1 = -> Assembly [_020_150mm_v007.Edge119,_020_150mm_v007.Edge119]
  Reference2 = -> Assembly [_020_150mm_v006.Edge14,_020_150mm_v006.Edge14]
FEATURE [App::FeaturePython] Joint012  label="Fixed012"  # Assembly joint (typed FeaturePython)
  Activated = true
  AngleMax = 0
  AngleMin = 0
  Detach1 = false
  Detach2 = false
  Distance = 0
  Distance2 = 0
  EnableAngleMax = false
  EnableAngleMin = false
  EnableLengthMax = false
  EnableLengthMin = false
  JointType = 0 (Fixed)
  LengthMax = 0
  LengthMin = 0
  Offset2 = pos=(0,0,0) rot=(0,0,1;1.5708rad)
  Placement1 = pos=(-10,-7,0) rot=(0.57735,0.57735,0.57735;4.18879rad)
  Placement2 = pos=(-10,7,150) rot=(1,0,0;4.71239rad)
  Reference1 = -> Assembly [_020_150mm_v008.Edge109,_020_150mm_v008.Edge109]
  Reference2 = -> Assembly [_020_150mm_v007.Edge28,_020_150mm_v007.Edge28]
FEATURE [App::FeaturePython] Joint013  label="Fixed013"  # Assembly joint (typed FeaturePython)
  Activated = true
  AngleMax = 0
  AngleMin = 0
  Detach1 = false
  Detach2 = false
  Distance = 0
  Distance2 = 0
  EnableAngleMax = false
  EnableAngleMin = false
  EnableLengthMax = false
  EnableLengthMin = false
  JointType = 0 (Fixed)
  LengthMax = 0
  LengthMin = 0
  Offset2 = pos=(0,0,0) rot=(0,0,-1;1.5708rad)
  Placement1 = pos=(10,-7,-1.8e-15) rot=(-0.57735,-0.57735,0.57735;4.18879rad)
  Placement2 = pos=(10,-7,0) rot=(0,-0.707107,0.707107;3.14159rad)
  Reference1 = -> Assembly [_020_150mm_v009.Edge92,_020_150mm_v009.Edge92]
  Reference2 = -> Assembly [_020_150mm_v006.Edge92,_020_150mm_v006.Edge92]
FEATURE [Assembly::JointGroup] Joints
  Group = -> [GroundedJoint,Joint,Joint001,Joint002,Joint003,Joint005,Joint006,Joint010,Joint011,Joint012,Joint013]
FEATURE [Assembly::AssemblyObject] Assembly  label="frame"
  Group = -> [Joints,_020_150mm_v2,_020_150mm_v003,GroundedJoint,Joint,_020_150mm_v004,Joint001,_020_150mm_v005,Joint002,_020_250mm_v2,Joint003,_020_250mm_v003,_020_250mm_v004,Joint005,_020_150mm_v006,Joint006,_020_150mm_v007,_020_150mm_v008,_020_150mm_v009,Joint010,Joint011,Joint012,Joint013]
  Origin = -> Origin
  Type = Assembly
---- part frame/corner-mount.FCStd = doc fcstd_a27adde6c6a2 ----
FCSTD DOCUMENT  (FreeCAD 1.0R39109 (Git))
Label: corner-mount
License: All rights reserved
objects: App::Link×7, App::FeaturePython×7, Sketcher::SketchObject×3, PartDesign::Pad×3, PartDesign::Chamfer×2, PartDesign::Body×1, Part::FeaturePython×1, Assembly::JointGroup×1, Assembly::AssemblyObject×1
note: 23 computed .brp shape members not serialized (recipe doc carries the construction recipe); baked Part::Feature solids carry a one-line shape summary decoded from their .brp

FEATURE [Sketcher::SketchObject] Sketch
  ArcFitTolerance = 1e-06
  AttachmentSupport = -> [XZ_Plane]
  FullyConstrained = true
  MakeInternals = false
  MapMode = 5
  Placement = pos=(0,0,0) rot=(1,0,0;1.5708rad)
  sketch-geometry (11):
    g0: LineSegment StartX=0 StartY=0 StartZ=0 EndX=44 EndY=0 EndZ=0
    g1: LineSegment StartX=44 StartY=0 StartZ=0 EndX=44 EndY=24 EndZ=0
    g2: LineSegment StartX=0 StartY=0 StartZ=0 EndX=0 EndY=44 EndZ=0
    g3: LineSegment StartX=0 StartY=44 StartZ=0 EndX=24 EndY=44 EndZ=0
    g4: LineSegment StartX=24 StartY=44 StartZ=0 EndX=44 EndY=24 EndZ=0
    g5: LineSegment [constr] StartX=24 StartY=44 StartZ=0 EndX=14 EndY=44 EndZ=0
    g6: LineSegment [constr] StartX=14 StartY=44 StartZ=0 EndX=14 EndY=34 EndZ=0
    g7: Circle CenterX=14 CenterY=34 CenterZ=0 NormalX=0 NormalY=0 NormalZ=1 AngleXU=0 Radius=2.6
    g8: LineSegment [constr] StartX=44 StartY=24 StartZ=0 EndX=44 EndY=14 EndZ=0
    g9: LineSegment [constr] StartX=44 StartY=14 StartZ=0 EndX=34 EndY=14 EndZ=0
    g10: Circle CenterX=34 CenterY=14 CenterZ=0 NormalX=0 NormalY=0 NormalZ=1 AngleXU=0 Radius=2.6
  constraints (30):
    c: Distance(g0) = 44
    c: Coincident(g0,g-1)
    c: PointOnObject(g0,g-1)
    c: Distance(g1) = 24
    c: Coincident(g1,g0)
    c: Vertical(g1)
    c: Distance(g2) = 44
    c: Coincident(g2,g0)
    c: PointOnObject(g2,g-2)
    c: Distance(g3) = 24
    c: Coincident(g3,g2)
    c: Horizontal(g3)
    c: Coincident(g4,g3)
    c: Coincident(g4,g1)
    c: Distance(g5) = 10
    c: Coincident(g5,g3)
    c: PointOnObject(g5,g3)
    c: Distance(g6) = 10
    c: Coincident(g6,g5)
    c: Vertical(g6)
    c: Diameter(g7) = 5.2
    c: Coincident(g7,g6)
    c: Distance(g8) = 10
    c: Coincident(g8,g1)
    c: PointOnObject(g8,g1)
    c: Distance(g9) = 10
    c: Coincident(g9,g8)
    c: Horizontal(g9)
    c: Diameter(g10) = 5.2
    c: Coincident(g10,g9)
FEATURE [PartDesign::Pad] Pad
  Direction = (0,-1,2e-16)
  Length = 4
  Length2 = 10
  Placement = pos=(0,0,0) rot=(1,0,0;1.5708rad)
  Profile = -> Sketch
  ReferenceAxis = -> Sketch [N_Axis]
  Refine = true
  Suppressed = false
  Type = 0
FEATURE [Sketcher::SketchObject] Sketch001
  ArcFitTolerance = 1e-06
  AttachmentSupport = -> [Pad]
  FullyConstrained = true
  MakeInternals = false
  MapMode = 5
  Placement = pos=(0,0,0) rot=(0.707107,0,-0.707107;3.14159rad)
  sketch-geometry (11):
    g0: LineSegment StartX=0 StartY=0 StartZ=0 EndX=0 EndY=44 EndZ=0
    g1: LineSegment StartX=0 StartY=0 StartZ=0 EndX=-44 EndY=0 EndZ=0
    g2: LineSegment StartX=-44 StartY=0 StartZ=0 EndX=-44 EndY=24 EndZ=0
    g3: LineSegment StartX=0 StartY=44 StartZ=0 EndX=-24 EndY=44 EndZ=0
    g4: LineSegment StartX=-44 StartY=24 StartZ=0 EndX=-24 EndY=44 EndZ=0
    g5: LineSegment [constr] StartX=-24 StartY=44 StartZ=0 EndX=-14 EndY=44 EndZ=0
    g6: LineSegment [constr] StartX=-14 StartY=44 StartZ=0 EndX=-14 EndY=34 EndZ=0
    g7: LineSegment [constr] StartX=-44 StartY=24 StartZ=0 EndX=-44 EndY=14 EndZ=0
    g8: LineSegment [constr] StartX=-44 StartY=14 StartZ=0 EndX=-34 EndY=14 EndZ=0
    g9: Circle CenterX=-34 CenterY=14 CenterZ=0 NormalX=0 NormalY=0 NormalZ=1 AngleXU=0 Radius=2.6
    g10: Circle CenterX=-14 CenterY=34 CenterZ=0 NormalX=0 NormalY=0 NormalZ=1 AngleXU=0 Radius=2.6
  constraints (30):
    c: Distance(g0) = 44
    c: Coincident(g0,g-1)
    c: PointOnObject(g0,g-2)
    c: Distance(g1) = 44
    c: Coincident(g1,g0)
    c: PointOnObject(g1,g-1)
    c: Distance(g2) = 24
    c: Coincident(g2,g1)
    c: Vertical(g2)
    c: Distance(g3) = 24
    c: Coincident(g3,g0)
    c: Horizontal(g3)
    c: Coincident(g4,g2)
    c: Coincident(g4,g3)
    c: Distance(g5) = 10
    c: Coincident(g5,g3)
    c: PointOnObject(g5,g3)
    c: Distance(g6) = 10
    c: Coincident(g6,g5)
    c: Vertical(g6)
    c: Distance(g7) = 10
    c: Coincident(g7,g2)
    c: PointOnObject(g7,g2)
    c: Distance(g8) = 10
    c: Coincident(g8,g7)
    c: Horizontal(g8)
    c: Diameter(g9) = 5.2
    c: Coincident(g9,g8)
    c: Diameter(g10) = 5.2
    c: Coincident(g10,g6)
FEATURE [PartDesign::Pad] Pad001
  BaseFeature = -> Pad
  Direction = (-1,0,-2e-16)
  Length = 4
  Length2 = 10
  Placement = pos=(0,0,0) rot=(1,0,0;1.5708rad)
  Profile = -> Sketch001
  ReferenceAxis = -> Sketch001 [N_Axis]
  Refine = true
  Reversed = true
  Suppressed = false
  Type = 0
FEATURE [Sketcher::SketchObject] Sketch002
  ArcFitTolerance = 1e-06
  AttachmentSupport = -> [Pad001]
  FullyConstrained = true
  MakeInternals = false
  MapMode = 5
  Placement = pos=(0,0,5e-16) rot=(1,0,0;3.14159rad)
  sketch-geometry (11):
    g0: LineSegment StartX=0 StartY=0 StartZ=0 EndX=0 EndY=44 EndZ=0
    g1: LineSegment StartX=0 StartY=44 StartZ=0 EndX=24 EndY=44 EndZ=0
    g2: LineSegment StartX=0 StartY=0 StartZ=0 EndX=44 EndY=0 EndZ=0
    g3: LineSegment StartX=44 StartY=0 StartZ=0 EndX=44 EndY=24 EndZ=0
    g4: LineSegment StartX=24 StartY=44 StartZ=0 EndX=44 EndY=24 EndZ=0
    g5: LineSegment [constr] StartX=24 StartY=44 StartZ=0 EndX=14 EndY=44 EndZ=0
    g6: LineSegment [constr] StartX=44 StartY=24 StartZ=0 EndX=44 EndY=14 EndZ=0
    g7: LineSegment [constr] StartX=14 StartY=44 StartZ=0 EndX=14 EndY=34 EndZ=0
    g8: LineSegment [constr] StartX=44 StartY=14 StartZ=0 EndX=34 EndY=14 EndZ=0
    g9: Circle CenterX=14 CenterY=34 CenterZ=0 NormalX=0 NormalY=0 NormalZ=1 AngleXU=0 Radius=2.6
    g10: Circle CenterX=34 CenterY=14 CenterZ=0 NormalX=0 NormalY=0 NormalZ=1 AngleXU=0 Radius=2.6
  constraints (30):
    c: Distance(g0) = 44
    c: Coincident(g0,g-1)
    c: PointOnObject(g0,g-2)
    c: Distance(g1) = 24
    c: Coincident(g1,g0)
    c: Horizontal(g1)
    c: Distance(g2) = 44
    c: Coincident(g2,g0)
    c: PointOnObject(g2,g-1)
    c: Distance(g3) = 24
    c: Coincident(g3,g2)
    c: Vertical(g3)
    c: Coincident(g4,g1)
    c: Coincident(g4,g3)
    c: Distance(g5) = 10
    c: Coincident(g5,g1)
    c: PointOnObject(g5,g1)
    c: Distance(g6) = 10
    c: Coincident(g6,g3)
    c: PointOnObject(g6,g3)
    c: Distance(g7) = 10
    c: Coincident(g7,g5)
    c: Vertical(g7)
    c: Distance(g8) = 10
    c: Coincident(g8,g6)
    c: Horizontal(g8)
    c: Diameter(g9) = 5.2
    c: Coincident(g9,g7)
    c: Diameter(g10) = 5.2
    c: Coincident(g10,g8)
FEATURE [PartDesign::Pad] Pad002
  BaseFeature = -> Pad001
  Direction = (0,0,-1)
  Length = 4
  Length2 = 10
  Placement = pos=(0,0,0) rot=(1,0,0;1.5708rad)
  Profile = -> Sketch002
  ReferenceAxis = -> Sketch002 [N_Axis]
  Refine = true
  Reversed = true
  Suppressed = false
  Type = 0
FEATURE [PartDesign::Chamfer] Chamfer
  Angle = 45
  Base = -> Pad002 [Edge2,Edge1,Edge23,Edge36,Edge18,Edge17]
  BaseFeature = -> Pad002
  ChamferType = 0
  FlipDirection = false
  Placement = pos=(0,0,0) rot=(1,0,0;1.5708rad)
  Refine = true
  Size = 2
  Size2 = 1
  SupportTransform = false
  Suppressed = false
  UseAllEdges = false
FEATURE [PartDesign::Chamfer] Chamfer001
  Angle = 45
  Base = -> Chamfer [Edge8,Edge7,Edge28]
  BaseFeature = -> Chamfer
  ChamferType = 0
  FlipDirection = false
  Placement = pos=(0,0,0) rot=(1,0,0;1.5708rad)
  Refine = true
  Size = 3
  Size2 = 1
  SupportTransform = false
  Suppressed = false
  UseAllEdges = false
FEATURE [PartDesign::Body] Body
  AllowCompound = false
  Group = -> [Sketch,Pad,Sketch001,Pad001,Sketch002,Pad002,Chamfer,Chamfer001]
  Origin = -> Origin
  Tip = -> Chamfer001
FEATURE [Part::FeaturePython] Screw  label="M5x10-Screw"  # WARN: FeaturePython — macro-defined, semantics opaque (R4)
  Diameter = 3
  Invert = false
  LeftHanded = false
  Length = 1
  LengthCustom = 10
  MatchOuter = false
  OffsetAngle = 0
  Thread = false
  Type = 85
FEATURE [App::Link] M5x10_Screw  label="M5x10-Screw001"
  LinkPlacement = pos=(34,-14,-3.1e-15) rot=(1,0,0;3.14159rad)
  LinkedObject = -> Screw
  Placement = pos=(34,-14,-3.1e-15) rot=(1,0,0;3.14159rad)
FEATURE [App::Link] Body001
  LinkedObject = -> Body
FEATURE [App::FeaturePython] GroundedJoint  # Assembly grounded joint (typed FeaturePython)
  ObjectToGround = -> Body001
FEATURE [App::FeaturePython] Joint  label="Fixed"  # Assembly joint (typed FeaturePython)
  Activated = true
  AngleMax = 0
  AngleMin = 0
  Detach1 = false
  Detach2 = false
  Distance = 0
  Distance2 = 0
  EnableAngleMax = false
  EnableAngleMin = false
  EnableLengthMax = false
  EnableLengthMin = false
  JointType = 0 (Fixed)
  LengthMax = 0
  LengthMin = 0
  Placement2 = pos=(34,-14,-3.1e-15) rot=(1,0,0;3.14159rad)
  Reference1 = -> Assembly [M5x10_Screw.Edge5,M5x10_Screw.Edge5]
  Reference2 = -> Assembly [Body001.Edge40,Body001.Edge40]
FEATURE [App::Link] M5x10_Screw001  label="M5x10-Screw002"
  LinkPlacement = pos=(0,-34,14) rot=(-0.707107,0,0.707107;3.14159rad)
  LinkedObject = -> Screw
  Placement = pos=(0,-34,14) rot=(-0.707107,0,0.707107;3.14159rad)
FEATURE [App::Link] M5x10_Screw002  label="M5x10-Screw003"
  LinkPlacement = pos=(0,-14,34) rot=(0.707107,0,-0.707107;3.14159rad)
  LinkedObject = -> Screw
  Placement = pos=(0,-14,34) rot=(0.707107,0,-0.707107;3.14159rad)
FEATURE [App::Link] M5x10_Screw003  label="M5x10-Screw004"
  LinkPlacement = pos=(14,-7.5e-15,34) rot=(-1,0,0;1.5708rad)
  LinkedObject = -> Screw
  Placement = pos=(14,-7.5e-15,34) rot=(-1,0,0;1.5708rad)
FEATURE [App::Link] M5x10_Screw004  label="M5x10-Screw005"
  LinkPlacement = pos=(34,-3.1e-15,14) rot=(-1,0,0;1.5708rad)
  LinkedObject = -> Screw
  Placement = pos=(34,-3.1e-15,14) rot=(-1,0,0;1.5708rad)
FEATURE [App::Link] M5x10_Screw005  label="M5x10-Screw006"
  LinkPlacement = pos=(14,-34,-7.6e-15) rot=(1,0,0;3.14159rad)
  LinkedObject = -> Screw
  Placement = pos=(14,-34,-7.6e-15) rot=(1,0,0;3.14159rad)
FEATURE [App::FeaturePython] Joint001  label="Fixed001"  # Assembly joint (typed FeaturePython)
  Activated = true
  AngleMax = 0
  AngleMin = 0
  Detach1 = false
  Detach2 = false
  Distance = 0
  Distance2 = 0
  EnableAngleMax = false
  EnableAngleMin = false
  EnableLengthMax = false
  EnableLengthMin = false
  JointType = 0 (Fixed)
  LengthMax = 0
  LengthMin = 0
  Placement2 = pos=(14,-34,-7.6e-15) rot=(1,0,0;3.14159rad)
  Reference1 = -> Assembly [M5x10_Screw005.Edge5,M5x10_Screw005.Edge5]
  Reference2 = -> Assembly [Body001.Edge41,Body001.Edge41]
FEATURE [App::FeaturePython] Joint002  label="Fixed002"  # Assembly joint (typed FeaturePython)
  Activated = true
  AngleMax = 0
  AngleMin = 0
  Detach1 = false
  Detach2 = false
  Distance = 0
  Distance2 = 0
  EnableAngleMax = false
  EnableAngleMin = false
  EnableLengthMax = false
  EnableLengthMin = false
  JointType = 0 (Fixed)
  LengthMax = 0
  LengthMin = 0
  Placement2 = pos=(34,-3.1e-15,14) rot=(1,0,0;1.5708rad)
  Reference1 = -> Assembly [M5x10_Screw004.Edge5,M5x10_Screw004.Edge5]
  Reference2 = -> Assembly [Body001.Edge58,Body001.Edge58]
FEATURE [App::FeaturePython] Joint003  label="Fixed003"  # Assembly joint (typed FeaturePython)
  Activated = true
  AngleMax = 0
  AngleMin = 0
  Detach1 = false
  Detach2 = false
  Distance = 0
  Distance2 = 0
  EnableAngleMax = false
  EnableAngleMin = false
  EnableLengthMax = false
  EnableLengthMin = false
  JointType = 0 (Fixed)
  LengthMax = 0
  LengthMin = 0
  Placement2 = pos=(14,-7.6e-15,34) rot=(1,0,0;1.5708rad)
  Reference1 = -> Assembly [M5x10_Screw003.Edge5,M5x10_Screw003.Edge5]
  Reference2 = -> Assembly [Body001.Edge59,Body001.Edge59]
FEATURE [App::FeaturePython] Joint004  label="Fixed004"  # Assembly joint (typed FeaturePython)
  Activated = true
  AngleMax = 0
  AngleMin = 0
  Detach1 = false
  Detach2 = false
  Distance = 0
  Distance2 = 0
  EnableAngleMax = false
  EnableAngleMin = false
  EnableLengthMax = false
  EnableLengthMin = false
  JointType = 0 (Fixed)
  LengthMax = 0
  LengthMin = 0
  Placement2 = pos=(0,-34,14) rot=(-0.707107,0,0.707107;3.14159rad)
  Reference1 = -> Assembly [M5x10_Screw001.Edge5,M5x10_Screw001.Edge5]
  Reference2 = -> Assembly [Body001.Edge8,Body001.Edge8]
FEATURE [App::FeaturePython] Joint005  label="Fixed005"  # Assembly joint (typed FeaturePython)
  Activated = true
  AngleMax = 0
  AngleMin = 0
  Detach1 = false
  Detach2 = false
  Distance = 0
  Distance2 = 0
  EnableAngleMax = false
  EnableAngleMin = false
  EnableLengthMax = false
  EnableLengthMin = false
  JointType = 0 (Fixed)
  LengthMax = 0
  LengthMin = 0
  Placement2 = pos=(0,-14,34) rot=(-0.707107,0,0.707107;3.14159rad)
  Reference1 = -> Assembly [M5x10_Screw002.Edge5,M5x10_Screw002.Edge5]
  Reference2 = -> Assembly [Body001.Edge9,Body001.Edge9]
FEATURE [Assembly::JointGroup] Joints
  Group = -> [GroundedJoint,Joint,Joint001,Joint002,Joint003,Joint004,Joint005]
FEATURE [Assembly::AssemblyObject] Assembly  label="corner-mount"
  Group = -> [Joints,M5x10_Screw,Body001,GroundedJoint,Joint,M5x10_Screw001,M5x10_Screw002,M5x10_Screw003,M5x10_Screw004,M5x10_Screw005,Joint001,Joint002,Joint003,Joint004,Joint005]
  Origin = -> Origin001
  Type = Assembly
---- part power-supply/psu-mount.FCStd = doc fcstd_d18cd55fd949 ----
FCSTD DOCUMENT  (FreeCAD 1.0R39109 (Git))
Label: psu-mount
License: All rights reserved
objects: App::Link×14, App::FeaturePython×14, Part::FeaturePython×4, Sketcher::SketchObject×2, PartDesign::Pad×2, PartDesign::Chamfer×1, PartDesign::Body×1, Part::Feature×1, Assembly::JointGroup×1, Assembly::AssemblyObject×1
note: 19 computed .brp shape members not serialized (recipe doc carries the construction recipe); baked Part::Feature solids carry a one-line shape summary decoded from their .brp

FEATURE [Sketcher::SketchObject] Sketch
  ArcFitTolerance = 1e-06
  AttachmentSupport = -> [XY_Plane]
  FullyConstrained = true
  MakeInternals = false
  MapMode = 5
  sketch-geometry (56):
    g0: LineSegment [constr] StartX=0 StartY=0 StartZ=0 EndX=190 EndY=0 EndZ=0
    g1: LineSegment [constr] StartX=190 StartY=0 StartZ=0 EndX=190 EndY=150 EndZ=0
    g2: LineSegment [constr] StartX=190 StartY=150 StartZ=0 EndX=0 EndY=150 EndZ=0
    g3: LineSegment [constr] StartX=0 StartY=150 StartZ=0 EndX=0 EndY=0 EndZ=0
    g4: LineSegment [constr] StartX=0 StartY=0 StartZ=0 EndX=42 EndY=0 EndZ=0
    g5: LineSegment [constr] StartX=42 StartY=0 StartZ=0 EndX=42 EndY=42 EndZ=0
    g6: LineSegment [constr] StartX=42 StartY=42 StartZ=0 EndX=0 EndY=42 EndZ=0
    g7: LineSegment [constr] StartX=0 StartY=42 StartZ=0 EndX=0 EndY=0 EndZ=0
    g8: LineSegment [constr] StartX=0 StartY=150 StartZ=0 EndX=0 EndY=108 EndZ=0
    g9: LineSegment [constr] StartX=0 StartY=108 StartZ=0 EndX=42 EndY=108 EndZ=0
    g10: LineSegment [constr] StartX=42 StartY=108 StartZ=0 EndX=42 EndY=150 EndZ=0
    g11: LineSegment [constr] StartX=42 StartY=150 StartZ=0 EndX=0 EndY=150 EndZ=0
    g12: LineSegment [constr] StartX=190 StartY=150 StartZ=0 EndX=148 EndY=150 EndZ=0
    g13: LineSegment [constr] StartX=148 StartY=150 StartZ=0 EndX=148 EndY=108 EndZ=0
    g14: LineSegment [constr] StartX=148 StartY=108 StartZ=0 EndX=190 EndY=108 EndZ=0
    g15: LineSegment [constr] StartX=190 StartY=108 StartZ=0 EndX=190 EndY=150 EndZ=0
    g16: LineSegment [constr] StartX=190 StartY=0 StartZ=0 EndX=190 EndY=42 EndZ=0
    g17: LineSegment [constr] StartX=190 StartY=42 StartZ=0 EndX=148 EndY=42 EndZ=0
    g18: LineSegment [constr] StartX=148 StartY=42 StartZ=0 EndX=148 EndY=0 EndZ=0
    g19: LineSegment [constr] StartX=148 StartY=0 StartZ=0 EndX=190 EndY=0 EndZ=0
    g20: LineSegment StartX=42 StartY=129 StartZ=0 EndX=21 EndY=108 EndZ=0
    g21: LineSegment StartX=21 StartY=108 StartZ=0 EndX=0 EndY=108 EndZ=0
    g22: LineSegment StartX=0 StartY=108 StartZ=0 EndX=0 EndY=42 EndZ=0
    g23: LineSegment StartX=0 StartY=42 StartZ=0 EndX=21 EndY=42 EndZ=0
    g24: LineSegment StartX=21 StartY=42 StartZ=0 EndX=42 EndY=21 EndZ=0
    g25: LineSegment StartX=42 StartY=21 StartZ=0 EndX=42 EndY=0 EndZ=0
    g26: LineSegment StartX=42 StartY=0 StartZ=0 EndX=148 EndY=0 EndZ=0
    g27: LineSegment StartX=148 StartY=0 StartZ=0 EndX=148 EndY=21 EndZ=0
    g28: LineSegment StartX=148 StartY=21 StartZ=0 EndX=169 EndY=42 EndZ=0
    g29: LineSegment StartX=169 StartY=42 StartZ=0 EndX=190 EndY=42 EndZ=0
    g30: LineSegment StartX=190 StartY=42 StartZ=0 EndX=190 EndY=108 EndZ=0
    g31: LineSegment StartX=190 StartY=108 StartZ=0 EndX=169 EndY=108 EndZ=0
    g32: LineSegment StartX=169 StartY=108 StartZ=0 EndX=148 EndY=129 EndZ=0
    g33: LineSegment StartX=148 StartY=129 StartZ=0 EndX=148 EndY=150 EndZ=0
    g34: LineSegment StartX=148 StartY=150 StartZ=0 EndX=42 EndY=150 EndZ=0
    g35: LineSegment StartX=42 StartY=150 StartZ=0 EndX=42 EndY=129 EndZ=0
    g36: LineSegment [constr] StartX=95 StartY=129 StartZ=0 EndX=95 EndY=150 EndZ=0
    g37: LineSegment [constr] StartX=95 StartY=139.5 StartZ=0 EndX=42 EndY=139.5 EndZ=0
    g38: Circle CenterX=68.5 CenterY=139.5 CenterZ=0 NormalX=0 NormalY=0 NormalZ=1 AngleXU=0 Radius=2.6
    g39: LineSegment [constr] StartX=95 StartY=139.5 StartZ=0 EndX=148 EndY=139.5 EndZ=0
    g40: Circle CenterX=121.5 CenterY=139.5 CenterZ=0 NormalX=0 NormalY=0 NormalZ=1 AngleXU=0 Radius=2.6
    g41: LineSegment [constr] StartX=0 StartY=75 StartZ=0 EndX=21 EndY=75 EndZ=0
    g42: LineSegment [constr] StartX=10.5 StartY=75 StartZ=0 EndX=10.5 EndY=108 EndZ=0
    g43: LineSegment [constr] StartX=10.5 StartY=75 StartZ=0 EndX=10.5 EndY=42 EndZ=0
    g44: Circle CenterX=10.5 CenterY=91.5 CenterZ=0 NormalX=0 NormalY=0 NormalZ=1 AngleXU=0 Radius=2.6
    g45: Circle CenterX=10.5 CenterY=58.5 CenterZ=0 NormalX=0 NormalY=0 NormalZ=1 AngleXU=0 Radius=2.6
    g46: LineSegment [constr] StartX=95 StartY=21 StartZ=0 EndX=95 EndY=0 EndZ=0
    g47: LineSegment [constr] StartX=95 StartY=10.5 StartZ=0 EndX=42 EndY=10.5 EndZ=0
    g48: LineSegment [constr] StartX=95 StartY=10.5 StartZ=0 EndX=148 EndY=10.5 EndZ=0
    g49: Circle CenterX=68.5 CenterY=10.5 CenterZ=0 NormalX=0 NormalY=0 NormalZ=1 AngleXU=0 Radius=2.6
    g50: Circle CenterX=121.5 CenterY=10.5 CenterZ=0 NormalX=0 NormalY=0 NormalZ=1 AngleXU=0 Radius=2.6
    g51: LineSegment [constr] StartX=169 StartY=75 StartZ=0 EndX=190 EndY=75 EndZ=0
    g52: LineSegment [constr] StartX=179.5 StartY=75 StartZ=0 EndX=179.5 EndY=42 EndZ=0
    g53: LineSegment [constr] StartX=179.5 StartY=75 StartZ=0 EndX=179.5 EndY=108 EndZ=0
    g54: Circle CenterX=179.5 CenterY=91.5 CenterZ=0 NormalX=0 NormalY=0 NormalZ=1 AngleXU=0 Radius=2.6
    g55: Circle CenterX=179.5 CenterY=58.5 CenterZ=0 NormalX=0 NormalY=0 NormalZ=1 AngleXU=0 Radius=2.6
  constraints (127):
    c: Coincident(g0,g1)
    c: Coincident(g1,g2)
    c: Coincident(g2,g3)
    c: Coincident(g3,g0)
    c: Horizontal(g0)
    c: Horizontal(g2)
    c: Vertical(g1)
    c: Vertical(g3)
    c: Distance(g1,g3) = 190
    c: Distance(g0,g2) = 150
    c: Coincident(g0,g-1)
    c: Coincident(g4,g5)
    c: Coincident(g5,g6)
    c: Coincident(g6,g7)
    c: Coincident(g7,g4)
    c: Horizontal(g4)
    c: Horizontal(g6)
    c: Vertical(g5)
    c: Vertical(g7)
    c: Distance(g5,g7) = 42
    c: Distance(g4,g6) = 42
    c: Coincident(g4,g0)
    c: Coincident(g8,g9)
    c: Coincident(g9,g10)
    c: Coincident(g10,g11)
    c: Coincident(g11,g8)
    c: Vertical(g8)
    c: Vertical(g10)
    c: Horizontal(g9)
    c: Horizontal(g11)
    c: Distance(g8,g10) = 42
    c: Distance(g9,g11) = 42
    c: Coincident(g8,g2)
    c: Coincident(g12,g13)
    c: Coincident(g13,g14)
    c: Coincident(g14,g15)
    c: Coincident(g15,g12)
    c: Horizontal(g12)
    c: Horizontal(g14)
    c: Vertical(g13)
    c: Vertical(g15)
    c: Distance(g13,g15) = 42
    c: Distance(g12,g14) = 42
    c: Coincident(g12,g1)
    c: Coincident(g16,g17)
    c: Coincident(g17,g18)
    c: Coincident(g18,g19)
    c: Coincident(g19,g16)
    c: Vertical(g16)
    c: Vertical(g18)
    c: Horizontal(g17)
    c: Horizontal(g19)
    c: Distance(g16,g18) = 42
    c: Distance(g17,g19) = 42
    c: Coincident(g16,g0)
    c: Symmetric(g10,g10,g20)
    c: Symmetric(g9,g9,g20)
    c: Coincident(g21,g20)
    c: Coincident(g21,g8)
    c: Coincident(g22,g8)
    c: Coincident(g22,g6)
    c: Coincident(g23,g6)
    c: Symmetric(g6,g6,g23)
    c: Coincident(g24,g23)
    c: Symmetric(g5,g5,g24)
    c: Coincident(g25,g24)
    c: Coincident(g25,g4)
    c: Coincident(g26,g4)
    c: Coincident(g26,g18)
    c: Coincident(g27,g18)
    c: Symmetric(g18,g18,g27)
    c: Coincident(g28,g27)
    c: Symmetric(g17,g17,g28)
    c: Coincident(g29,g28)
    c: Coincident(g29,g16)
    c: Coincident(g30,g16)
    c: Coincident(g30,g14)
    c: Coincident(g31,g14)
    c: Symmetric(g14,g14,g31)
    c: Coincident(g32,g31)
    c: Symmetric(g13,g13,g32)
    c: Coincident(g33,g32)
    c: Coincident(g33,g12)
    c: Coincident(g34,g12)
    c: Coincident(g34,g10)
    c: Coincident(g35,g10)
    c: Coincident(g35,g20)
    c: Symmetric(g20,g32,g36)
    c: Symmetric(g34,g34,g36)
    c: Symmetric(g36,g36,g37)
    c: Symmetric(g35,g35,g37)
    c: Diameter(g38) = 5.2
    c: Symmetric(g37,g37,g38)
    c: Coincident(g39,g37)
    c: Symmetric(g33,g33,g39)
    c: Diameter(g40) = 5.2
    c: Symmetric(g39,g39,g40)
    c: Symmetric(g22,g22,g41)
    c: Symmetric(g20,g23,g41)
    c: Symmetric(g41,g41,g42)
    c: Symmetric(g21,g21,g42)
    c: Coincident(g43,g42)
    c: Symmetric(g23,g23,g43)
    c: Diameter(g44) = 5.2
    c: Symmetric(g42,g42,g44)
    c: Diameter(g45) = 5.2
    c: Symmetric(g43,g43,g45)
    c: Symmetric(g24,g27,g46)
    c: Symmetric(g26,g26,g46)
    c: Symmetric(g46,g46,g47)
    c: Symmetric(g25,g25,g47)
    c: Coincident(g48,g47)
    c: Symmetric(g27,g27,g48)
    c: Diameter(g49) = 5.2
    c: Symmetric(g47,g47,g49)
    c: Diameter(g50) = 5.2
    c: Symmetric(g48,g48,g50)
    c: Symmetric(g31,g28,g51)
    c: Symmetric(g30,g30,g51)
    c: Symmetric(g51,g51,g52)
    c: Symmetric(g29,g29,g52)
    c: Coincident(g53,g52)
    c: Symmetric(g31,g31,g53)
    c: Diameter(g54) = 5.2
    c: Symmetric(g53,g53,g54)
    c: Diameter(g55) = 5.2
    c: Symmetric(g52,g52,g55)
FEATURE [PartDesign::Pad] Pad
  Direction = (0,0,1)
  Length = 4
  Length2 = 10
  Profile = -> Sketch
  ReferenceAxis = -> Sketch [N_Axis]
  Refine = true
  Suppressed = false
  Type = 0
FEATURE [PartDesign::Chamfer] Chamfer
  Angle = 45
  Base = -> Pad [Edge1,Edge2,Edge11,Edge14,Edge23,Edge26,Edge38,Edge35]
  BaseFeature = -> Pad
  ChamferType = 0
  FlipDirection = false
  Refine = true
  Size = 3
  Size2 = 1
  SupportTransform = false
  Suppressed = false
  UseAllEdges = false
FEATURE [Sketcher::SketchObject] Sketch001
  ArcFitTolerance = 1e-06
  AttachmentSupport = -> [Chamfer]
  FullyConstrained = true
  MakeInternals = false
  MapMode = 5
  Placement = pos=(0,0,4) rot=(0,0,1;0rad)
  sketch-geometry (16):
    g0: LineSegment [constr] StartX=0 StartY=0 StartZ=0 EndX=190 EndY=0 EndZ=0
    g1: LineSegment [constr] StartX=190 StartY=0 StartZ=0 EndX=190 EndY=150 EndZ=0
    g2: LineSegment [constr] StartX=190 StartY=150 StartZ=0 EndX=0 EndY=150 EndZ=0
    g3: LineSegment [constr] StartX=0 StartY=150 StartZ=0 EndX=0 EndY=0 EndZ=0
    g4: LineSegment [constr] StartX=0 StartY=150 StartZ=0 EndX=0 EndY=110 EndZ=0
    g5: LineSegment [constr] StartX=0 StartY=110 StartZ=0 EndX=48 EndY=110 EndZ=0
    g6: LineSegment [constr] StartX=48 StartY=110 StartZ=0 EndX=48 EndY=150 EndZ=0
    g7: LineSegment [constr] StartX=48 StartY=150 StartZ=0 EndX=0 EndY=150 EndZ=0
    g8: Circle CenterX=48 CenterY=110 CenterZ=0 NormalX=0 NormalY=0 NormalZ=1 AngleXU=0 Radius=5
    g9: Circle CenterX=48 CenterY=110 CenterZ=0 NormalX=0 NormalY=0 NormalZ=1 AngleXU=0 Radius=2.4
    g10: LineSegment [constr] StartX=48 StartY=110 StartZ=0 EndX=48 EndY=40 EndZ=0
    g11: LineSegment [constr] StartX=48 StartY=40 StartZ=0 EndX=140.5 EndY=40 EndZ=0
    g12: LineSegment [constr] StartX=140.5 StartY=40 StartZ=0 EndX=140.5 EndY=110 EndZ=0
    g13: LineSegment [constr] StartX=140.5 StartY=110 StartZ=0 EndX=48 EndY=110 EndZ=0
    g14: Circle CenterX=140.5 CenterY=40 CenterZ=0 NormalX=0 NormalY=0 NormalZ=1 AngleXU=0 Radius=2.4
    g15: Circle CenterX=140.5 CenterY=40 CenterZ=0 NormalX=0 NormalY=0 NormalZ=1 AngleXU=0 Radius=5
  constraints (41):
    c: Coincident(g0,g1)
    c: Coincident(g1,g2)
    c: Coincident(g2,g3)
    c: Coincident(g3,g0)
    c: Horizontal(g0)
    c: Horizontal(g2)
    c: Vertical(g1)
    c: Vertical(g3)
    c: Distance(g1,g3) = 190
    c: Distance(g0,g2) = 150
    c: Coincident(g0,g-1)
    c: Coincident(g4,g5)
    c: Coincident(g5,g6)
    c: Coincident(g6,g7)
    c: Coincident(g7,g4)
    c: Vertical(g4)
    c: Vertical(g6)
    c: Horizontal(g5)
    c: Horizontal(g7)
    c: Distance(g4,g6) = 48
    c: Distance(g5,g7) = 40
    c: Coincident(g4,g2)
    c: Diameter(g8) = 10
    c: Coincident(g8,g5)
    c: Diameter(g9) = 4.8
    c: Coincident(g9,g5)
    c: Coincident(g10,g11)
    c: Coincident(g11,g12)
    c: Coincident(g12,g13)
    c: Coincident(g13,g10)
    c: Vertical(g10)
    c: Vertical(g12)
    c: Horizontal(g11)
    c: Horizontal(g13)
    c: Distance(g10,g12) = 92.5
    c: Distance(g11,g13) = 70
    c: Coincident(g10,g5)
    c: Diameter(g14) = 4.8
    c: Coincident(g14,g11)
    c: Diameter(g15) = 10
    c: Coincident(g15,g11)
FEATURE [PartDesign::Pad] Pad001
  BaseFeature = -> Chamfer
  Direction = (0,0,1)
  Length = 6
  Length2 = 10
  Profile = -> Sketch001
  ReferenceAxis = -> Sketch001 [N_Axis]
  Refine = true
  Suppressed = false
  Type = 0
FEATURE [PartDesign::Body] Body  label="mount"
  AllowCompound = false
  Group = -> [Sketch,Pad,Chamfer,Sketch001,Pad001]
  Origin = -> Origin
  Tip = -> Pad001
FEATURE [Part::FeaturePython] Screw  label="M5x10-Screw"  # WARN: FeaturePython — macro-defined, semantics opaque (R4)
  Diameter = 3
  Invert = false
  LeftHanded = false
  Length = 1
  LengthCustom = 10
  MatchOuter = false
  OffsetAngle = 0
  Placement = pos=(-71,0,0) rot=(0,0,1;0rad)
  Thread = true
  Type = 85
FEATURE [Part::FeaturePython] TSlot  label="M5 x 30/40 series-TSlot"  # WARN: FeaturePython — macro-defined, semantics opaque (R4)
  Diameter = 3
  Invert = false
  LeftHanded = false
  MatchOuter = false
  OffsetAngle = 0
  Placement = pos=(0,0,-40) rot=(0,0,1;0rad)
  SlotWidth = 1
  Thread = true
  Type = 1
FEATURE [Part::FeaturePython] Insert  label="M3x5.74-Insert"  # WARN: FeaturePython — macro-defined, semantics opaque (R4)
  Diameter = 3
  ExternalDiam = 4.55
  Invert = false
  LeftHanded = false
  Length = 5.74
  MatchOuter = false
  OffsetAngle = 0
  Placement = pos=(0,0,-102) rot=(0,0,1;0rad)
  Thread = true
  Type = 0
FEATURE [App::Link] mount  label="mount001"
  LinkedObject = -> Body
FEATURE [App::Link] M3x5_74_Insert  label="M3x5.74-Insert001"
  LinkPlacement = pos=(48,110,10.0967) rot=(0,0,1;0rad)
  LinkedObject = -> Insert
  Placement = pos=(48,110,10.0967) rot=(0,0,1;0rad)
FEATURE [App::Link] M3x5_74_Insert001  label="M3x5.74-Insert002"
  LinkPlacement = pos=(140.5,40,10.0967) rot=(0,0,1;0rad)
  LinkedObject = -> Insert
  Placement = pos=(140.5,40,10.0967) rot=(0,0,1;0rad)
FEATURE [App::FeaturePython] GroundedJoint  # Assembly grounded joint (typed FeaturePython)
  ObjectToGround = -> mount
FEATURE [App::FeaturePython] Joint  label="Fixed"  # Assembly joint (typed FeaturePython)
  Activated = true
  AngleMax = 0
  AngleMin = 0
  Detach1 = false
  Detach2 = false
  Distance = 0
  Distance2 = 0
  EnableAngleMax = false
  EnableAngleMin = false
  EnableLengthMax = false
  EnableLengthMin = false
  JointType = 0 (Fixed)
  LengthMax = 0
  LengthMin = 0
  Offset2 = pos=(0,0,-5) rot=(0,0,1;0rad)
  Placement1 = pos=(0,0,-5.09667) rot=(0,0,1;0rad)
  Placement2 = pos=(140.5,40,5) rot=(0,0,1;0rad)
  Reference1 = -> Assembly [M3x5_74_Insert001.Edge298,M3x5_74_Insert001.Edge298]
  Reference2 = -> Assembly [mount.Edge103,mount.Edge103]
FEATURE [App::FeaturePython] Joint001  label="Fixed001"  # Assembly joint (typed FeaturePython)
  Activated = true
  AngleMax = 0
  AngleMin = 0
  Detach1 = false
  Detach2 = false
  Distance = 0
  Distance2 = 0
  EnableAngleMax = false
  EnableAngleMin = false
  EnableLengthMax = false
  EnableLengthMin = false
  JointType = 0 (Fixed)
  LengthMax = 0
  LengthMin = 0
  Offset2 = pos=(0,0,-5) rot=(0,0,1;0rad)
  Placement1 = pos=(0,0,-5.09667) rot=(0,0,1;0rad)
  Placement2 = pos=(48,110,5) rot=(0,0,1;0rad)
  Reference1 = -> Assembly [M3x5_74_Insert.Edge298,M3x5_74_Insert.Edge298]
  Reference2 = -> Assembly [mount.Edge104,mount.Edge104]
FEATURE [App::Link] M5x10_Screw  label="M5x10-Screw001"
  LinkPlacement = pos=(68.5,10.5,0) rot=(1,0,0;3.14159rad)
  LinkedObject = -> Screw
  Placement = pos=(68.5,10.5,0) rot=(1,0,0;3.14159rad)
FEATURE [App::FeaturePython] Joint002  label="Fixed002"  # Assembly joint (typed FeaturePython)
  Activated = true
  AngleMax = 0
  AngleMin = 0
  Detach1 = false
  Detach2 = false
  Distance = 0
  Distance2 = 0
  EnableAngleMax = false
  EnableAngleMin = false
  EnableLengthMax = false
  EnableLengthMin = false
  JointType = 0 (Fixed)
  LengthMax = 0
  LengthMin = 0
  Placement2 = pos=(68.5,10.5,0) rot=(0,0,1;0rad)
  Reference1 = -> Assembly [M5x10_Screw.Edge5,M5x10_Screw.Edge5]
  Reference2 = -> Assembly [mount.Edge35,mount.Edge35]
FEATURE [App::Link] M5x10_Screw002  label="M5x10-Screw003"
  LinkPlacement = pos=(179.5,58.5,0) rot=(1,0,0;3.14159rad)
  LinkedObject = -> Screw
  Placement = pos=(179.5,58.5,0) rot=(1,0,0;3.14159rad)
FEATURE [App::Link] M5x10_Screw003  label="M5x10-Screw004"
  LinkPlacement = pos=(179.5,91.5,0) rot=(1,0,0;3.14159rad)
  LinkedObject = -> Screw
  Placement = pos=(179.5,91.5,0) rot=(1,0,0;3.14159rad)
FEATURE [App::Link] M5x10_Screw004  label="M5x10-Screw005"
  LinkPlacement = pos=(121.5,139.5,0) rot=(1,0,0;3.14159rad)
  LinkedObject = -> Screw
  Placement = pos=(121.5,139.5,0) rot=(1,0,0;3.14159rad)
FEATURE [App::Link] M5x10_Screw005  label="M5x10-Screw006"
  LinkPlacement = pos=(68.5,139.5,0) rot=(1,0,0;3.14159rad)
  LinkedObject = -> Screw
  Placement = pos=(68.5,139.5,0) rot=(1,0,0;3.14159rad)
FEATURE [App::Link] M5x10_Screw006  label="M5x10-Screw007"
  LinkPlacement = pos=(10.5,58.5,0) rot=(1,0,0;3.14159rad)
  LinkedObject = -> Screw
  Placement = pos=(10.5,58.5,0) rot=(1,0,0;3.14159rad)
FEATURE [App::FeaturePython] Joint004  label="Fixed004"  # Assembly joint (typed FeaturePython)
  Activated = true
  AngleMax = 0
  AngleMin = 0
  Detach1 = false
  Detach2 = false
  Distance = 0
  Distance2 = 0
  EnableAngleMax = false
  EnableAngleMin = false
  EnableLengthMax = false
  EnableLengthMin = false
  JointType = 0 (Fixed)
  LengthMax = 0
  LengthMin = 0
  Placement2 = pos=(179.5,58.5,0) rot=(0,0,1;0rad)
  Reference1 = -> Assembly [M5x10_Screw002.Edge5,M5x10_Screw002.Edge5]
  Reference2 = -> Assembly [mount.Edge30,mount.Edge30]
FEATURE [App::FeaturePython] Joint005  label="Fixed005"  # Assembly joint (typed FeaturePython)
  Activated = true
  AngleMax = 0
  AngleMin = 0
  Detach1 = false
  Detach2 = false
  Distance = 0
  Distance2 = 0
  EnableAngleMax = false
  EnableAngleMin = false
  EnableLengthMax = false
  EnableLengthMin = false
  JointType = 0 (Fixed)
  LengthMax = 0
  LengthMin = 0
  Placement2 = pos=(179.5,91.5,0) rot=(0,0,1;0rad)
  Reference1 = -> Assembly [M5x10_Screw003.Edge5,M5x10_Screw003.Edge5]
  Reference2 = -> Assembly [mount.Edge28,mount.Edge28]
FEATURE [App::FeaturePython] Joint006  label="Fixed006"  # Assembly joint (typed FeaturePython)
  Activated = true
  AngleMax = 0
  AngleMin = 0
  Detach1 = false
  Detach2 = false
  Distance = 0
  Distance2 = 0
  EnableAngleMax = false
  EnableAngleMin = false
  EnableLengthMax = false
  EnableLengthMin = false
  JointType = 0 (Fixed)
  LengthMax = 0
  LengthMin = 0
  Placement2 = pos=(121.5,139.5,0) rot=(0,0,1;0rad)
  Reference1 = -> Assembly [M5x10_Screw004.Edge5,M5x10_Screw004.Edge5]
  Reference2 = -> Assembly [mount.Edge31,mount.Edge31]
FEATURE [App::FeaturePython] Joint007  label="Fixed007"  # Assembly joint (typed FeaturePython)
  Activated = true
  AngleMax = 0
  AngleMin = 0
  Detach1 = false
  Detach2 = false
  Distance = 0
  Distance2 = 0
  EnableAngleMax = false
  EnableAngleMin = false
  EnableLengthMax = false
  EnableLengthMin = false
  JointType = 0 (Fixed)
  LengthMax = 0
  LengthMin = 0
  Placement2 = pos=(68.5,139.5,0) rot=(0,0,1;0rad)
  Reference1 = -> Assembly [M5x10_Screw005.Edge5,M5x10_Screw005.Edge5]
  Reference2 = -> Assembly [mount.Edge32,mount.Edge32]
FEATURE [App::FeaturePython] Joint008  label="Fixed008"  # Assembly joint (typed FeaturePython)
  Activated = true
  AngleMax = 0
  AngleMin = 0
  Detach1 = false
  Detach2 = false
  Distance = 0
  Distance2 = 0
  EnableAngleMax = false
  EnableAngleMin = false
  EnableLengthMax = false
  EnableLengthMin = false
  JointType = 0 (Fixed)
  LengthMax = 0
  LengthMin = 0
  Placement2 = pos=(10.5,58.5,0) rot=(0,0,1;0rad)
  Reference1 = -> Assembly [M5x10_Screw006.Edge5,M5x10_Screw006.Edge5]
  Reference2 = -> Assembly [mount.Edge33,mount.Edge33]
FEATURE [App::Link] M5x10_Screw007  label="M5x10-Screw008"
  LinkPlacement = pos=(10.5,91.5,0) rot=(1,0,0;3.14159rad)
  LinkedObject = -> Screw
  Placement = pos=(10.5,91.5,0) rot=(1,0,0;3.14159rad)
FEATURE [App::FeaturePython] Joint009  label="Fixed009"  # Assembly joint (typed FeaturePython)
  Activated = true
  AngleMax = 0
  AngleMin = 0
  Detach1 = false
  Detach2 = false
  Distance = 0
  Distance2 = 0
  EnableAngleMax = false
  EnableAngleMin = false
  EnableLengthMax = false
  EnableLengthMin = false
  JointType = 0 (Fixed)
  LengthMax = 0
  LengthMin = 0
  Placement2 = pos=(10.5,91.5,0) rot=(0,0,1;0rad)
  Reference1 = -> Assembly [M5x10_Screw007.Edge5,M5x10_Screw007.Edge5]
  Reference2 = -> Assembly [mount.Edge29,mount.Edge29]
FEATURE [App::Link] M5x10_Screw008  label="M5x10-Screw009"
  LinkPlacement = pos=(121.5,10.5,0) rot=(1,0,0;3.14159rad)
  LinkedObject = -> Screw
  Placement = pos=(121.5,10.5,0) rot=(1,0,0;3.14159rad)
FEATURE [App::FeaturePython] Joint016  label="Fixed016"  # Assembly joint (typed FeaturePython)
  Activated = true
  AngleMax = 0
  AngleMin = 0
  Detach1 = false
  Detach2 = false
  Distance = 0
  Distance2 = 0
  EnableAngleMax = false
  EnableAngleMin = false
  EnableLengthMax = false
  EnableLengthMin = false
  JointType = 0 (Fixed)
  LengthMax = 0
  LengthMin = 0
  Placement2 = pos=(121.5,10.5,0) rot=(0,0,1;0rad)
  Reference1 = -> Assembly [M5x10_Screw008.Edge5,M5x10_Screw008.Edge5]
  Reference2 = -> Assembly [mount.Edge34,mount.Edge34]
FEATURE [Part::Feature] Part__Feature  label="MW LRS-50-24"
  shape: bbox 99 x 30 x 82 mm, 1343 faces (baked)
FEATURE [App::Link] MW_LRS_50_24  label="MW LRS-50-025"
  LinkPlacement = pos=(43.5,33.5,10) rot=(1,0,0;1.5708rad)
  LinkedObject = -> Part__Feature
  Placement = pos=(43.5,33.5,10) rot=(1,0,0;1.5708rad)
FEATURE [App::FeaturePython] Joint019  label="Fixed019"  # Assembly joint (typed FeaturePython)
  Activated = true
  AngleMax = 0
  AngleMin = 0
  Detach1 = false
  Detach2 = false
  Distance = 0
  Distance2 = 0
  EnableAngleMax = false
  EnableAngleMin = false
  EnableLengthMax = false
  EnableLengthMin = false
  JointType = 0 (Fixed)
  LengthMax = 0
  LengthMin = 0
  Offset2 = pos=(0,0,0) rot=(0,0,-1;1.5708rad)
  Placement1 = pos=(4.5,-1.8e-15,-76.5) rot=(-0.57735,-0.57735,-0.57735;2.0944rad)
  Placement2 = pos=(48,110,10) rot=(0,0,-1;1.5708rad)
  Reference1 = -> Assembly [MW_LRS_50_24.Edge1250,MW_LRS_50_24.Edge1250]
  Reference2 = -> Assembly [mount.Edge104,mount.Edge104]
FEATURE [Part::FeaturePython] Screw001  label="M3x6-Screw"  # WARN: FeaturePython — macro-defined, semantics opaque (R4)
  Diameter = 1
  Invert = false
  LeftHanded = false
  Length = 9
  LengthCustom = 6
  MatchOuter = false
  OffsetAngle = 0
  Thread = true
  Type = 85
FEATURE [App::Link] M3x6_Screw  label="M3x6-Screw001"
  LinkPlacement = pos=(48,110,11) rot=(0,0,1;4.71239rad)
  LinkedObject = -> Screw001
  Placement = pos=(48,110,11) rot=(0,0,1;4.71239rad)
FEATURE [App::FeaturePython] Joint020  label="Fixed020"  # Assembly joint (typed FeaturePython)
  Activated = true
  AngleMax = 0
  AngleMin = 0
  Detach1 = false
  Detach2 = false
  Distance = 0
  Distance2 = 0
  EnableAngleMax = false
  EnableAngleMin = false
  EnableLengthMax = false
  EnableLengthMin = false
  JointType = 0 (Fixed)
  LengthMax = 0
  LengthMin = 0
  Placement2 = pos=(4.5,1,-76.5) rot=(-0.57735,-0.57735,-0.57735;2.0944rad)
  Reference1 = -> Assembly [M3x6_Screw.Edge5,M3x6_Screw.Edge5]
  Reference2 = -> Assembly [MW_LRS_50_24.Edge1313,MW_LRS_50_24.Edge1313]
FEATURE [App::Link] M3x6_Screw001  label="M3x6-Screw002"
  LinkPlacement = pos=(140.5,40,11) rot=(0,0,-1;1.5708rad)
  LinkedObject = -> Screw001
  Placement = pos=(140.5,40,11) rot=(0,0,-1;1.5708rad)
FEATURE [App::FeaturePython] Joint021  label="Revolute021"  # Assembly joint (typed FeaturePython)
  Activated = true
  AngleMax = 0
  AngleMin = 0
  Detach1 = false
  Detach2 = false
  Distance = 0
  Distance2 = 0
  EnableAngleMax = false
  EnableAngleMin = false
  EnableLengthMax = false
  EnableLengthMin = false
  JointType = 1 (Revolute)
  LengthMax = 0
  LengthMin = 0
  Placement2 = pos=(97,1,-6.5) rot=(-0.57735,-0.57735,-0.57735;2.0944rad)
  Reference1 = -> Assembly [M3x6_Screw001.Edge5,M3x6_Screw001.Edge5]
  Reference2 = -> Assembly [MW_LRS_50_24.Edge1311,MW_LRS_50_24.Edge1311]
FEATURE [Assembly::JointGroup] Joints
  Group = -> [GroundedJoint,Joint,Joint001,Joint002,Joint004,Joint005,Joint006,Joint007,Joint008,Joint009,Joint016,Joint019,Joint020,Joint021]
FEATURE [Assembly::AssemblyObject] Assembly  label="psu-mount"
  Group = -> [Joints,mount,M3x5_74_Insert,M3x5_74_Insert001,GroundedJoint,Joint,Joint001,M5x10_Screw,Joint002,M5x10_Screw002,M5x10_Screw003,M5x10_Screw004,M5x10_Screw005,M5x10_Screw006,Joint004,Joint005,Joint006,Joint007,Joint008,M5x10_Screw007,Joint009,M5x10_Screw008,Joint016,MW_LRS_50_24,Joint019,M3x6_Screw,Joint020,M3x6_Screw001,Joint021]
  Origin = -> Origin001
  Type = Assembly
